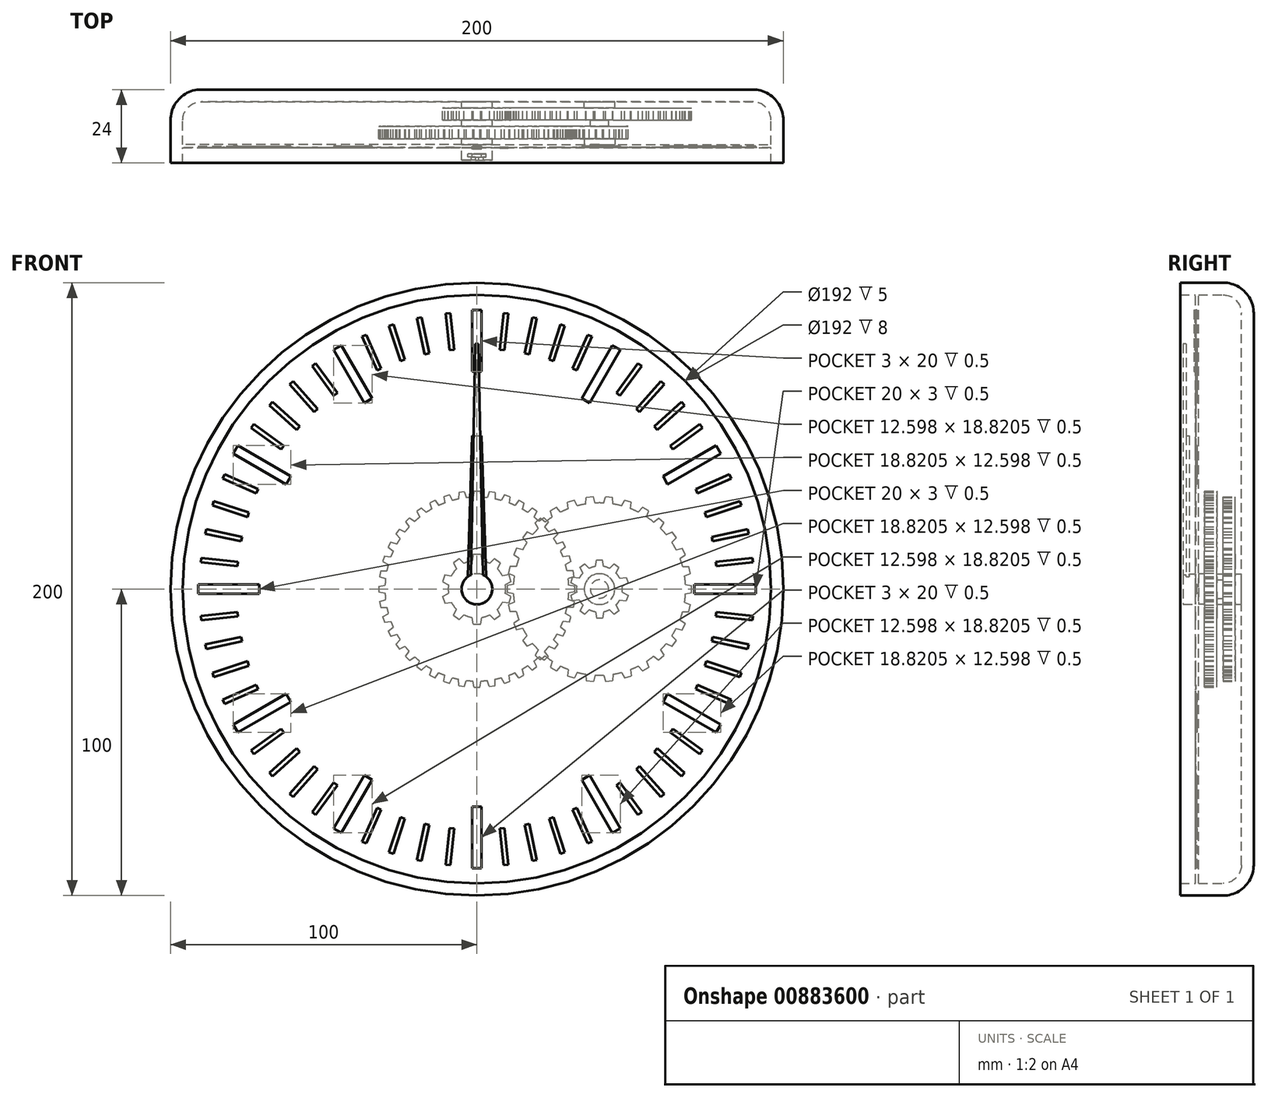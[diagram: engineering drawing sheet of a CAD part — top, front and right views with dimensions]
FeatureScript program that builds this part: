
annotation { "Feature Type Name" : "Feature", "Feature Type Description" : "" }
export const myFeature = defineFeature(function(context is Context, id is Id, definition is map)
    precondition{}
    {
        {
            var Q0;
            Q0=qCreatedBy(makeId("Front.planeOp"),FACE);
            var sketch = newSketch(context, id + "F0", { "sketchPlane" : qUnion([Q0])});
            skCircle(sketch, "E0", {"center": v(0, 0) * mm, "radius": 100 * mm});
            skSolve(sketch);
        }
        {
            var Q0;
            Q0 = qSketchRegion(id + "F0", true);
            extrude(context, id + "F1", {"entities" : qUnion([Q0]), "depth" : 24 * mm, "offsetDistance" : 25 * mm});
        }
        {
            var Q0;
            Q0=makeQuery(id+"F1.opExtrude","CAP_EDGE",EDGE,{"disambiguationData":[OSD([sQuery(id+"F0.wireOp",EDGE,"E0")])],"isStart":true});
            fillet(context, id + "F2", {"entities" : qUnion([Q0]), "radius" : 10 * mm, "tangentPropagation" : true, "allowEdgeOverflow" : false});
        }
        {
            var Q0;
            Q0=makeQuery(id+"F1.opExtrude","CAP_FACE",FACE,{"disambiguationData":[OSD([sQuery(id+"F0.wireOp",EDGE,"E0")])],"isStart":false});
            shell(context, id + "F3", {"entities" : qUnion([Q0]), "thickness" : 4 * mm});
        }
        {
            var Q0;
            {var subQ0=sQuery(id+"F0.wireOp",EDGE,"E0");Q0=makeQuery(id+"F3.opShell","OFFSET_FACE",FACE,{"disambiguationData":[OSD([subQ0]),TDD([makeQuery(id+"F1.opExtrude","CAP_FACE",FACE,{"disambiguationData":[OSD([subQ0])],"isStart":true})])]});}
            var sketch = newSketch(context, id + "F4", { "sketchPlane" : qUnion([Q0])});
            skCircle(sketch, "E1", {"center": v(0, 0) * mm, "radius": 3 * mm});
            skCircle(sketch, "E2", {"center": v(0, 0) * mm, "radius": 5 * mm});
            skCircle(sketch, "E3", {"center": v(40, 0) * mm, "radius": 3 * mm});
            skCircle(sketch, "E4", {"center": v(40, 0) * mm, "radius": 5 * mm});
            skSolve(sketch);
        }
        {
            var Q0;
            Q0 = qSketchRegion(id + "F4", true);
            extrude(context, id + "F5", {"entities" : qUnion([Q0]), "operationType" : NewBodyOperationType.ADD, "depth" : 2 * mm, "offsetDistance" : 25 * mm});
        }
        {
            var Q0;
            {var subQ0=sQuery(id+"F0.wireOp",EDGE,"E0");Q0=makeQuery(id+"F5.boolean.opBoolean","SPLIT",FACE,{"disambiguationData":[TD([makeQuery(id+"F5.opExtrude","SWEPT_FACE",FACE,{"disambiguationData":[OSD([sQuery(id+"F4.wireOp",EDGE,"E1")])]})])],"derivedFrom":makeQuery(id+"F3.opShell","OFFSET_FACE",FACE,{"disambiguationData":[OSD([subQ0]),TDD([makeQuery(id+"F1.opExtrude","CAP_FACE",FACE,{"disambiguationData":[OSD([subQ0])],"isStart":true})])]})});}
            extrude(context, id + "F6", {"entities" : qUnion([Q0]), "depth" : 19 * mm, "offsetDistance" : 25 * mm});
        }
        {
            var Q0;
            {var subQ0=sQuery(id+"F0.wireOp",EDGE,"E0");Q0=makeQuery(id+"F5.boolean.opBoolean","SPLIT",FACE,{"disambiguationData":[TD([makeQuery(id+"F5.opExtrude","SWEPT_FACE",FACE,{"disambiguationData":[OSD([sQuery(id+"F4.wireOp",EDGE,"E3")])]})])],"derivedFrom":makeQuery(id+"F3.opShell","OFFSET_FACE",FACE,{"disambiguationData":[OSD([subQ0]),TDD([makeQuery(id+"F1.opExtrude","CAP_FACE",FACE,{"disambiguationData":[OSD([subQ0])],"isStart":true})])]})});}
            extrude(context, id + "F7", {"entities" : qUnion([Q0]), "depth" : 8 * mm, "offsetDistance" : 25 * mm});
        }
        {
            var Q0;
            Q0=makeQuery(id+"F5.opExtrude","CAP_FACE",FACE,{"disambiguationData":[OSD([sQuery(id+"F4.wireOp",EDGE,"E1"),sQuery(id+"F4.wireOp",EDGE,"E2")])],"isStart":false});
            var sketch = newSketch(context, id + "F8", { "sketchPlane" : qUnion([Q0])});
            skCircle(sketch, "E5", {"center": v(0, 0) * mm, "radius": 9.38 * mm});
            skLineSegment(sketch, "E6", {"start": v(0, 11.38) * mm, "end": v(1.18, 11.38) * mm});
            skLineSegment(sketch, "E7", {"start": v(1.18, 11.38) * mm, "end": v(1.55, 9.25) * mm});
            skLineSegment(sketch, "E8.MirrorCS", {"start": v(0, 11.38) * mm, "end": v(-1.18, 11.38) * mm});
            skLineSegment(sketch, "E9.MirrorCS", {"start": v(-1.18, 11.38) * mm, "end": v(-1.55, 9.25) * mm});
            skLineSegment(sketch, "E10.1.0", {"start": v(-7.64, 8.51) * mm, "end": v(-6.7, 6.57) * mm});
            skLineSegment(sketch, "E10.1.1", {"start": v(-6.69, 9.2) * mm, "end": v(-7.64, 8.51) * mm});
            skLineSegment(sketch, "E10.1.2", {"start": v(-6.69, 9.2) * mm, "end": v(-5.73, 9.9) * mm});
            skLineSegment(sketch, "E10.1.3", {"start": v(-5.73, 9.9) * mm, "end": v(-4.18, 8.4) * mm});
            skLineSegment(sketch, "E10.2.0", {"start": v(-11.18, 2.4) * mm, "end": v(-9.27, 1.38) * mm});
            skLineSegment(sketch, "E10.2.1", {"start": v(-10.82, 3.52) * mm, "end": v(-11.18, 2.4) * mm});
            skLineSegment(sketch, "E10.2.2", {"start": v(-10.82, 3.52) * mm, "end": v(-10.45, 4.64) * mm});
            skLineSegment(sketch, "E10.2.3", {"start": v(-10.45, 4.64) * mm, "end": v(-8.31, 4.33) * mm});
            skLineSegment(sketch, "E11.2.3.0", {"start": v(-10.45, -4.64) * mm, "end": v(-8.31, -4.33) * mm});
            skLineSegment(sketch, "E11.3.3.0", {"start": v(-10.82, -3.52) * mm, "end": v(-10.45, -4.64) * mm});
            skLineSegment(sketch, "E11.6.3.0", {"start": v(-10.82, -3.52) * mm, "end": v(-11.18, -2.4) * mm});
            skLineSegment(sketch, "E11.9.3.0", {"start": v(-11.18, -2.4) * mm, "end": v(-9.27, -1.38) * mm});
            skLineSegment(sketch, "E11.2.4.0", {"start": v(-5.73, -9.9) * mm, "end": v(-4.18, -8.4) * mm});
            skLineSegment(sketch, "E11.3.4.0", {"start": v(-6.69, -9.2) * mm, "end": v(-5.73, -9.9) * mm});
            skLineSegment(sketch, "E11.6.4.0", {"start": v(-6.69, -9.2) * mm, "end": v(-7.64, -8.51) * mm});
            skLineSegment(sketch, "E11.9.4.0", {"start": v(-7.64, -8.51) * mm, "end": v(-6.7, -6.57) * mm});
            skLineSegment(sketch, "E11.2.5.0", {"start": v(1.18, -11.38) * mm, "end": v(1.55, -9.25) * mm});
            skLineSegment(sketch, "E11.3.5.0", {"start": v(0, -11.38) * mm, "end": v(1.18, -11.38) * mm});
            skLineSegment(sketch, "E11.6.5.0", {"start": v(0, -11.38) * mm, "end": v(-1.18, -11.38) * mm});
            skLineSegment(sketch, "E11.9.5.0", {"start": v(-1.18, -11.38) * mm, "end": v(-1.55, -9.25) * mm});
            skLineSegment(sketch, "E11.2.6.0", {"start": v(7.64, -8.51) * mm, "end": v(6.7, -6.57) * mm});
            skLineSegment(sketch, "E11.3.6.0", {"start": v(6.69, -9.2) * mm, "end": v(7.64, -8.51) * mm});
            skLineSegment(sketch, "E11.6.6.0", {"start": v(6.69, -9.2) * mm, "end": v(5.73, -9.9) * mm});
            skLineSegment(sketch, "E11.9.6.0", {"start": v(5.73, -9.9) * mm, "end": v(4.18, -8.4) * mm});
            skLineSegment(sketch, "E11.2.7.0", {"start": v(11.18, -2.4) * mm, "end": v(9.27, -1.38) * mm});
            skLineSegment(sketch, "E11.3.7.0", {"start": v(10.82, -3.52) * mm, "end": v(11.18, -2.4) * mm});
            skLineSegment(sketch, "E11.6.7.0", {"start": v(10.82, -3.52) * mm, "end": v(10.45, -4.64) * mm});
            skLineSegment(sketch, "E11.9.7.0", {"start": v(10.45, -4.64) * mm, "end": v(8.31, -4.33) * mm});
            skLineSegment(sketch, "E11.2.8.0", {"start": v(10.45, 4.64) * mm, "end": v(8.31, 4.33) * mm});
            skLineSegment(sketch, "E11.3.8.0", {"start": v(10.82, 3.52) * mm, "end": v(10.45, 4.64) * mm});
            skLineSegment(sketch, "E11.6.8.0", {"start": v(10.82, 3.52) * mm, "end": v(11.18, 2.4) * mm});
            skLineSegment(sketch, "E11.9.8.0", {"start": v(11.18, 2.4) * mm, "end": v(9.27, 1.38) * mm});
            skLineSegment(sketch, "E11.2.9.0", {"start": v(5.73, 9.9) * mm, "end": v(4.18, 8.4) * mm});
            skLineSegment(sketch, "E11.3.9.0", {"start": v(6.69, 9.2) * mm, "end": v(5.73, 9.9) * mm});
            skLineSegment(sketch, "E11.6.9.0", {"start": v(6.69, 9.2) * mm, "end": v(7.64, 8.51) * mm});
            skLineSegment(sketch, "E11.9.9.0", {"start": v(7.64, 8.51) * mm, "end": v(6.7, 6.57) * mm});
            skSolve(sketch);
        }
        {
            var Q0;
            Q0 = qSketchRegion(id + "F8", true);
            extrude(context, id + "F9", {"entities" : qUnion([Q0]), "operationType" : NewBodyOperationType.ADD, "depth" : 4 * mm, "offsetDistance" : 25 * mm});
        }
        {
            var Q0;
            Q0=makeQuery(id+"F5.opExtrude","CAP_FACE",FACE,{"disambiguationData":[OSD([sQuery(id+"F4.wireOp",EDGE,"E3"),sQuery(id+"F4.wireOp",EDGE,"E4")])],"isStart":false});
            var sketch = newSketch(context, id + "F10", { "sketchPlane" : qUnion([Q0])});
            skCircle(sketch, "E12", {"center": v(40, 0) * mm, "radius": 28.12 * mm});
            skLineSegment(sketch, "E13", {"start": v(11.92, 1.54) * mm, "end": v(9.88, 1.18) * mm});
            skLineSegment(sketch, "E14", {"start": v(9.88, 1.18) * mm, "end": v(9.88, 0) * mm});
            skLineSegment(sketch, "E15.MirrorCS", {"start": v(9.88, -1.18) * mm, "end": v(9.88, 0) * mm});
            skLineSegment(sketch, "E16.MirrorCS", {"start": v(11.92, -1.54) * mm, "end": v(9.88, -1.18) * mm});
            skLineSegment(sketch, "E17.1.0", {"start": v(12.85, -7.34) * mm, "end": v(10.78, -7.42) * mm});
            skLineSegment(sketch, "E17.1.1", {"start": v(10.78, -7.42) * mm, "end": v(10.53, -6.26) * mm});
            skLineSegment(sketch, "E17.1.2", {"start": v(10.29, -5.11) * mm, "end": v(10.53, -6.26) * mm});
            skLineSegment(sketch, "E17.1.3", {"start": v(12.21, -4.33) * mm, "end": v(10.29, -5.11) * mm});
            skLineSegment(sketch, "E17.2.0", {"start": v(14.97, -12.83) * mm, "end": v(12.96, -13.33) * mm});
            skLineSegment(sketch, "E17.2.1", {"start": v(12.96, -13.33) * mm, "end": v(12.48, -12.25) * mm});
            skLineSegment(sketch, "E17.2.2", {"start": v(12, -11.18) * mm, "end": v(12.48, -12.25) * mm});
            skLineSegment(sketch, "E17.2.3", {"start": v(13.72, -10.02) * mm, "end": v(12, -11.18) * mm});
            skLineSegment(sketch, "E18.2.3.0", {"start": v(18.18, -17.75) * mm, "end": v(16.32, -18.66) * mm});
            skLineSegment(sketch, "E18.3.3.0", {"start": v(16.32, -18.66) * mm, "end": v(15.63, -17.7) * mm});
            skLineSegment(sketch, "E18.6.3.0", {"start": v(14.94, -16.75) * mm, "end": v(15.63, -17.7) * mm});
            skLineSegment(sketch, "E18.9.3.0", {"start": v(16.38, -15.26) * mm, "end": v(14.94, -16.75) * mm});
            skLineSegment(sketch, "E18.2.4.0", {"start": v(22.35, -21.9) * mm, "end": v(20.72, -23.18) * mm});
            skLineSegment(sketch, "E18.3.4.0", {"start": v(20.72, -23.18) * mm, "end": v(19.84, -22.39) * mm});
            skLineSegment(sketch, "E18.6.4.0", {"start": v(18.97, -21.6) * mm, "end": v(19.84, -22.39) * mm});
            skLineSegment(sketch, "E18.9.4.0", {"start": v(20.07, -19.84) * mm, "end": v(18.97, -21.6) * mm});
            skLineSegment(sketch, "E18.2.5.0", {"start": v(27.3, -25.09) * mm, "end": v(25.96, -26.68) * mm});
            skLineSegment(sketch, "E18.3.5.0", {"start": v(25.96, -26.68) * mm, "end": v(24.94, -26.09) * mm});
            skLineSegment(sketch, "E18.6.5.0", {"start": v(23.92, -25.5) * mm, "end": v(24.94, -26.09) * mm});
            skLineSegment(sketch, "E18.9.5.0", {"start": v(24.63, -23.55) * mm, "end": v(23.92, -25.5) * mm});
            skLineSegment(sketch, "E18.2.6.0", {"start": v(32.78, -27.18) * mm, "end": v(31.81, -29.01) * mm});
            skLineSegment(sketch, "E18.3.6.0", {"start": v(31.81, -29.01) * mm, "end": v(30.7, -28.65) * mm});
            skLineSegment(sketch, "E18.6.6.0", {"start": v(29.57, -28.29) * mm, "end": v(30.7, -28.65) * mm});
            skLineSegment(sketch, "E18.9.6.0", {"start": v(29.86, -26.23) * mm, "end": v(29.57, -28.29) * mm});
            skLineSegment(sketch, "E18.2.7.0", {"start": v(38.6, -28.09) * mm, "end": v(38.02, -30.08) * mm});
            skLineSegment(sketch, "E18.3.7.0", {"start": v(38.02, -30.08) * mm, "end": v(36.85, -29.96) * mm});
            skLineSegment(sketch, "E18.6.7.0", {"start": v(35.68, -29.84) * mm, "end": v(36.85, -29.96) * mm});
            skLineSegment(sketch, "E18.9.7.0", {"start": v(35.53, -27.77) * mm, "end": v(35.68, -29.84) * mm});
            skLineSegment(sketch, "E18.2.8.0", {"start": v(44.47, -27.77) * mm, "end": v(44.32, -29.84) * mm});
            skLineSegment(sketch, "E18.3.8.0", {"start": v(44.32, -29.84) * mm, "end": v(43.15, -29.96) * mm});
            skLineSegment(sketch, "E18.6.8.0", {"start": v(41.98, -30.08) * mm, "end": v(43.15, -29.96) * mm});
            skLineSegment(sketch, "E18.9.8.0", {"start": v(41.4, -28.09) * mm, "end": v(41.98, -30.08) * mm});
            skLineSegment(sketch, "E18.2.9.0", {"start": v(50.14, -26.23) * mm, "end": v(50.43, -28.29) * mm});
            skLineSegment(sketch, "E18.3.9.0", {"start": v(50.43, -28.29) * mm, "end": v(49.3, -28.65) * mm});
            skLineSegment(sketch, "E18.6.9.0", {"start": v(48.19, -29.01) * mm, "end": v(49.3, -28.65) * mm});
            skLineSegment(sketch, "E18.9.9.0", {"start": v(47.22, -27.18) * mm, "end": v(48.19, -29.01) * mm});
            skLineSegment(sketch, "E18.2.10.0", {"start": v(55.37, -23.55) * mm, "end": v(56.08, -25.5) * mm});
            skLineSegment(sketch, "E18.3.10.0", {"start": v(56.08, -25.5) * mm, "end": v(55.06, -26.09) * mm});
            skLineSegment(sketch, "E18.6.10.0", {"start": v(54.04, -26.68) * mm, "end": v(55.06, -26.09) * mm});
            skLineSegment(sketch, "E18.9.10.0", {"start": v(52.7, -25.09) * mm, "end": v(54.04, -26.68) * mm});
            skLineSegment(sketch, "E18.2.11.0", {"start": v(59.93, -19.84) * mm, "end": v(61.03, -21.6) * mm});
            skLineSegment(sketch, "E18.3.11.0", {"start": v(61.03, -21.6) * mm, "end": v(60.16, -22.39) * mm});
            skLineSegment(sketch, "E18.6.11.0", {"start": v(59.28, -23.18) * mm, "end": v(60.16, -22.39) * mm});
            skLineSegment(sketch, "E18.9.11.0", {"start": v(57.65, -21.9) * mm, "end": v(59.28, -23.18) * mm});
            skLineSegment(sketch, "E18.2.12.0", {"start": v(63.62, -15.26) * mm, "end": v(65.06, -16.75) * mm});
            skLineSegment(sketch, "E18.3.12.0", {"start": v(65.06, -16.75) * mm, "end": v(64.37, -17.7) * mm});
            skLineSegment(sketch, "E18.6.12.0", {"start": v(63.68, -18.66) * mm, "end": v(64.37, -17.7) * mm});
            skLineSegment(sketch, "E18.9.12.0", {"start": v(61.82, -17.75) * mm, "end": v(63.68, -18.66) * mm});
            skLineSegment(sketch, "E18.2.13.0", {"start": v(66.28, -10.02) * mm, "end": v(68, -11.18) * mm});
            skLineSegment(sketch, "E18.3.13.0", {"start": v(68, -11.18) * mm, "end": v(67.52, -12.25) * mm});
            skLineSegment(sketch, "E18.6.13.0", {"start": v(67.04, -13.33) * mm, "end": v(67.52, -12.25) * mm});
            skLineSegment(sketch, "E18.9.13.0", {"start": v(65.03, -12.83) * mm, "end": v(67.04, -13.33) * mm});
            skLineSegment(sketch, "E18.2.14.0", {"start": v(67.79, -4.33) * mm, "end": v(69.71, -5.11) * mm});
            skLineSegment(sketch, "E18.3.14.0", {"start": v(69.71, -5.11) * mm, "end": v(69.47, -6.26) * mm});
            skLineSegment(sketch, "E18.6.14.0", {"start": v(69.22, -7.42) * mm, "end": v(69.47, -6.26) * mm});
            skLineSegment(sketch, "E18.9.14.0", {"start": v(67.15, -7.34) * mm, "end": v(69.22, -7.42) * mm});
            skLineSegment(sketch, "E18.2.15.0", {"start": v(68.08, 1.54) * mm, "end": v(70.13, 1.18) * mm});
            skLineSegment(sketch, "E18.3.15.0", {"start": v(70.12, 1.18) * mm, "end": v(70.12, 0) * mm});
            skLineSegment(sketch, "E18.6.15.0", {"start": v(70.12, -1.18) * mm, "end": v(70.12, 0) * mm});
            skLineSegment(sketch, "E18.9.15.0", {"start": v(68.08, -1.54) * mm, "end": v(70.13, -1.18) * mm});
            skLineSegment(sketch, "E18.2.16.0", {"start": v(67.15, 7.34) * mm, "end": v(69.22, 7.42) * mm});
            skLineSegment(sketch, "E18.3.16.0", {"start": v(69.22, 7.42) * mm, "end": v(69.47, 6.26) * mm});
            skLineSegment(sketch, "E18.6.16.0", {"start": v(69.71, 5.11) * mm, "end": v(69.47, 6.26) * mm});
            skLineSegment(sketch, "E18.9.16.0", {"start": v(67.79, 4.33) * mm, "end": v(69.71, 5.11) * mm});
            skLineSegment(sketch, "E18.2.17.0", {"start": v(65.03, 12.83) * mm, "end": v(67.04, 13.33) * mm});
            skLineSegment(sketch, "E18.3.17.0", {"start": v(67.04, 13.33) * mm, "end": v(67.52, 12.25) * mm});
            skLineSegment(sketch, "E18.6.17.0", {"start": v(68, 11.18) * mm, "end": v(67.52, 12.25) * mm});
            skLineSegment(sketch, "E18.9.17.0", {"start": v(66.28, 10.02) * mm, "end": v(68, 11.18) * mm});
            skLineSegment(sketch, "E18.2.18.0", {"start": v(61.82, 17.75) * mm, "end": v(63.68, 18.66) * mm});
            skLineSegment(sketch, "E18.3.18.0", {"start": v(63.68, 18.66) * mm, "end": v(64.37, 17.7) * mm});
            skLineSegment(sketch, "E18.6.18.0", {"start": v(65.06, 16.75) * mm, "end": v(64.37, 17.7) * mm});
            skLineSegment(sketch, "E18.9.18.0", {"start": v(63.62, 15.26) * mm, "end": v(65.06, 16.75) * mm});
            skLineSegment(sketch, "E18.2.19.0", {"start": v(57.65, 21.9) * mm, "end": v(59.28, 23.18) * mm});
            skLineSegment(sketch, "E18.3.19.0", {"start": v(59.28, 23.18) * mm, "end": v(60.16, 22.39) * mm});
            skLineSegment(sketch, "E18.6.19.0", {"start": v(61.03, 21.6) * mm, "end": v(60.16, 22.39) * mm});
            skLineSegment(sketch, "E18.9.19.0", {"start": v(59.93, 19.84) * mm, "end": v(61.03, 21.6) * mm});
            skLineSegment(sketch, "E18.2.20.0", {"start": v(52.7, 25.09) * mm, "end": v(54.04, 26.68) * mm});
            skLineSegment(sketch, "E18.3.20.0", {"start": v(54.04, 26.68) * mm, "end": v(55.06, 26.09) * mm});
            skLineSegment(sketch, "E18.6.20.0", {"start": v(56.08, 25.5) * mm, "end": v(55.06, 26.09) * mm});
            skLineSegment(sketch, "E18.9.20.0", {"start": v(55.37, 23.55) * mm, "end": v(56.08, 25.5) * mm});
            skLineSegment(sketch, "E18.2.21.0", {"start": v(47.22, 27.18) * mm, "end": v(48.19, 29.01) * mm});
            skLineSegment(sketch, "E18.3.21.0", {"start": v(48.19, 29.01) * mm, "end": v(49.3, 28.65) * mm});
            skLineSegment(sketch, "E18.6.21.0", {"start": v(50.43, 28.29) * mm, "end": v(49.3, 28.65) * mm});
            skLineSegment(sketch, "E18.9.21.0", {"start": v(50.14, 26.23) * mm, "end": v(50.43, 28.29) * mm});
            skLineSegment(sketch, "E18.2.22.0", {"start": v(41.4, 28.09) * mm, "end": v(41.98, 30.08) * mm});
            skLineSegment(sketch, "E18.3.22.0", {"start": v(41.98, 30.08) * mm, "end": v(43.15, 29.96) * mm});
            skLineSegment(sketch, "E18.6.22.0", {"start": v(44.32, 29.84) * mm, "end": v(43.15, 29.96) * mm});
            skLineSegment(sketch, "E18.9.22.0", {"start": v(44.47, 27.77) * mm, "end": v(44.32, 29.84) * mm});
            skLineSegment(sketch, "E18.2.23.0", {"start": v(35.53, 27.77) * mm, "end": v(35.68, 29.84) * mm});
            skLineSegment(sketch, "E18.3.23.0", {"start": v(35.68, 29.84) * mm, "end": v(36.85, 29.96) * mm});
            skLineSegment(sketch, "E18.6.23.0", {"start": v(38.02, 30.08) * mm, "end": v(36.85, 29.96) * mm});
            skLineSegment(sketch, "E18.9.23.0", {"start": v(38.6, 28.09) * mm, "end": v(38.02, 30.08) * mm});
            skLineSegment(sketch, "E18.2.24.0", {"start": v(29.86, 26.23) * mm, "end": v(29.57, 28.29) * mm});
            skLineSegment(sketch, "E18.3.24.0", {"start": v(29.57, 28.29) * mm, "end": v(30.7, 28.65) * mm});
            skLineSegment(sketch, "E18.6.24.0", {"start": v(31.81, 29.01) * mm, "end": v(30.7, 28.65) * mm});
            skLineSegment(sketch, "E18.9.24.0", {"start": v(32.78, 27.18) * mm, "end": v(31.81, 29.01) * mm});
            skLineSegment(sketch, "E18.2.25.0", {"start": v(24.63, 23.55) * mm, "end": v(23.92, 25.5) * mm});
            skLineSegment(sketch, "E18.3.25.0", {"start": v(23.92, 25.5) * mm, "end": v(24.94, 26.09) * mm});
            skLineSegment(sketch, "E18.6.25.0", {"start": v(25.96, 26.68) * mm, "end": v(24.94, 26.09) * mm});
            skLineSegment(sketch, "E18.9.25.0", {"start": v(27.3, 25.09) * mm, "end": v(25.96, 26.68) * mm});
            skLineSegment(sketch, "E18.2.26.0", {"start": v(20.07, 19.84) * mm, "end": v(18.97, 21.6) * mm});
            skLineSegment(sketch, "E18.3.26.0", {"start": v(18.97, 21.6) * mm, "end": v(19.84, 22.39) * mm});
            skLineSegment(sketch, "E18.6.26.0", {"start": v(20.72, 23.18) * mm, "end": v(19.84, 22.39) * mm});
            skLineSegment(sketch, "E18.9.26.0", {"start": v(22.35, 21.9) * mm, "end": v(20.72, 23.18) * mm});
            skLineSegment(sketch, "E18.2.27.0", {"start": v(16.38, 15.26) * mm, "end": v(14.94, 16.75) * mm});
            skLineSegment(sketch, "E18.3.27.0", {"start": v(14.94, 16.75) * mm, "end": v(15.63, 17.7) * mm});
            skLineSegment(sketch, "E18.6.27.0", {"start": v(16.32, 18.66) * mm, "end": v(15.63, 17.7) * mm});
            skLineSegment(sketch, "E18.9.27.0", {"start": v(18.18, 17.75) * mm, "end": v(16.32, 18.66) * mm});
            skLineSegment(sketch, "E18.2.28.0", {"start": v(13.72, 10.02) * mm, "end": v(12, 11.18) * mm});
            skLineSegment(sketch, "E18.3.28.0", {"start": v(12, 11.18) * mm, "end": v(12.48, 12.25) * mm});
            skLineSegment(sketch, "E18.6.28.0", {"start": v(12.96, 13.33) * mm, "end": v(12.48, 12.25) * mm});
            skLineSegment(sketch, "E18.9.28.0", {"start": v(14.97, 12.83) * mm, "end": v(12.96, 13.33) * mm});
            skLineSegment(sketch, "E18.2.29.0", {"start": v(12.21, 4.33) * mm, "end": v(10.29, 5.11) * mm});
            skLineSegment(sketch, "E18.3.29.0", {"start": v(10.29, 5.11) * mm, "end": v(10.53, 6.26) * mm});
            skLineSegment(sketch, "E18.6.29.0", {"start": v(10.78, 7.42) * mm, "end": v(10.53, 6.26) * mm});
            skLineSegment(sketch, "E18.9.29.0", {"start": v(12.85, 7.34) * mm, "end": v(10.78, 7.42) * mm});
            skSolve(sketch);
        }
        {
            var Q0;
            Q0 = qSketchRegion(id + "F10", true);
            extrude(context, id + "F11", {"entities" : qUnion([Q0]), "operationType" : NewBodyOperationType.ADD, "depth" : 4 * mm, "offsetDistance" : 25 * mm});
        }
        {
            var Q0;
            Q0=makeQuery(id+"F9.opExtrude","CAP_FACE",FACE,{"disambiguationData":[OSD([sQuery(id+"F8.wireOp",EDGE,"E5"),sQuery(id+"F8.wireOp",EDGE,"E6"),sQuery(id+"F8.wireOp",EDGE,"E7"),sQuery(id+"F8.wireOp",EDGE,"E8.MirrorCS"),sQuery(id+"F8.wireOp",EDGE,"E9.MirrorCS"),sQuery(id+"F8.wireOp",EDGE,"E10.1.0"),sQuery(id+"F8.wireOp",EDGE,"E10.1.1"),sQuery(id+"F8.wireOp",EDGE,"E10.1.2"),sQuery(id+"F8.wireOp",EDGE,"E10.1.3"),sQuery(id+"F8.wireOp",EDGE,"E10.2.0"),sQuery(id+"F8.wireOp",EDGE,"E10.2.1"),sQuery(id+"F8.wireOp",EDGE,"E10.2.2"),sQuery(id+"F8.wireOp",EDGE,"E10.2.3"),sQuery(id+"F8.wireOp",EDGE,"E11.2.3.0"),sQuery(id+"F8.wireOp",EDGE,"E11.3.3.0"),sQuery(id+"F8.wireOp",EDGE,"E11.6.3.0"),sQuery(id+"F8.wireOp",EDGE,"E11.9.3.0"),sQuery(id+"F8.wireOp",EDGE,"E11.2.4.0"),sQuery(id+"F8.wireOp",EDGE,"E11.3.4.0"),sQuery(id+"F8.wireOp",EDGE,"E11.6.4.0"),sQuery(id+"F8.wireOp",EDGE,"E11.9.4.0"),sQuery(id+"F8.wireOp",EDGE,"E11.2.5.0"),sQuery(id+"F8.wireOp",EDGE,"E11.3.5.0"),sQuery(id+"F8.wireOp",EDGE,"E11.6.5.0"),sQuery(id+"F8.wireOp",EDGE,"E11.9.5.0"),sQuery(id+"F8.wireOp",EDGE,"E11.2.6.0"),sQuery(id+"F8.wireOp",EDGE,"E11.3.6.0"),sQuery(id+"F8.wireOp",EDGE,"E11.6.6.0"),sQuery(id+"F8.wireOp",EDGE,"E11.9.6.0"),sQuery(id+"F8.wireOp",EDGE,"E11.2.7.0"),sQuery(id+"F8.wireOp",EDGE,"E11.3.7.0"),sQuery(id+"F8.wireOp",EDGE,"E11.6.7.0"),sQuery(id+"F8.wireOp",EDGE,"E11.9.7.0"),sQuery(id+"F8.wireOp",EDGE,"E11.2.8.0"),sQuery(id+"F8.wireOp",EDGE,"E11.3.8.0"),sQuery(id+"F8.wireOp",EDGE,"E11.6.8.0"),sQuery(id+"F8.wireOp",EDGE,"E11.9.8.0"),sQuery(id+"F8.wireOp",EDGE,"E11.2.9.0"),sQuery(id+"F8.wireOp",EDGE,"E11.3.9.0"),sQuery(id+"F8.wireOp",EDGE,"E11.6.9.0"),sQuery(id+"F8.wireOp",EDGE,"E11.9.9.0")])],"isStart":false});
            var sketch = newSketch(context, id + "F12", { "sketchPlane" : qUnion([Q0])});
            skCircle(sketch, "E19.0", {"center": v(0, 0) * mm, "radius": 3 * mm});
            skCircle(sketch, "E20.0", {"center": v(0, 0) * mm, "radius": 5 * mm});
            skSolve(sketch);
        }
        {
            var Q0;
            Q0 = qSketchRegion(id + "F12", true);
            extrude(context, id + "F13", {"entities" : qUnion([Q0]), "depth" : 2 * mm, "offsetDistance" : 25 * mm});
        }
        {
            var Q0;
            Q0=makeQuery(id+"F13.opExtrude","CAP_FACE",FACE,{"disambiguationData":[OSD([sQuery(id+"F12.wireOp",EDGE,"E19.0"),sQuery(id+"F12.wireOp",EDGE,"E20.0")])],"isStart":false});
            var sketch = newSketch(context, id + "F14", { "sketchPlane" : qUnion([Q0])});
            skCircle(sketch, "E21.0.0", {"center": v(0, 0) * mm, "radius": 3 * mm});
            skCircle(sketch, "E22", {"center": v(0, 0) * mm, "radius": 30 * mm});
            skLineSegment(sketch, "E23", {"start": v(0, 32) * mm, "end": v(0.94, 32) * mm});
            skLineSegment(sketch, "E24", {"start": v(0.94, 32) * mm, "end": v(1.3, 29.97) * mm});
            skLineSegment(sketch, "E25.MirrorCS", {"start": v(0, 32) * mm, "end": v(-0.94, 32) * mm});
            skLineSegment(sketch, "E26.MirrorCS", {"start": v(-0.94, 32) * mm, "end": v(-1.3, 29.97) * mm});
            skLineSegment(sketch, "E27.1.0", {"start": v(-5.94, 31.46) * mm, "end": v(-5.97, 29.4) * mm});
            skLineSegment(sketch, "E27.1.1", {"start": v(-5, 31.6) * mm, "end": v(-5.94, 31.46) * mm});
            skLineSegment(sketch, "E27.1.2", {"start": v(-5, 31.6) * mm, "end": v(-4.08, 31.75) * mm});
            skLineSegment(sketch, "E27.1.3", {"start": v(-4.08, 31.75) * mm, "end": v(-3.4, 29.8) * mm});
            skLineSegment(sketch, "E27.2.0", {"start": v(-10.78, 30.14) * mm, "end": v(-10.5, 28.1) * mm});
            skLineSegment(sketch, "E27.2.1", {"start": v(-9.89, 30.43) * mm, "end": v(-10.78, 30.14) * mm});
            skLineSegment(sketch, "E27.2.2", {"start": v(-9.89, 30.43) * mm, "end": v(-9, 30.73) * mm});
            skLineSegment(sketch, "E27.2.3", {"start": v(-9, 30.73) * mm, "end": v(-8.03, 28.9) * mm});
            skLineSegment(sketch, "E28.2.3.0", {"start": v(-15.37, 28.08) * mm, "end": v(-14.77, 26.11) * mm});
            skLineSegment(sketch, "E28.3.3.0", {"start": v(-14.53, 28.51) * mm, "end": v(-15.37, 28.08) * mm});
            skLineSegment(sketch, "E28.6.3.0", {"start": v(-14.53, 28.51) * mm, "end": v(-13.69, 28.94) * mm});
            skLineSegment(sketch, "E28.9.3.0", {"start": v(-13.69, 28.94) * mm, "end": v(-12.45, 27.3) * mm});
            skLineSegment(sketch, "E28.2.4.0", {"start": v(-19.57, 25.33) * mm, "end": v(-18.67, 23.48) * mm});
            skLineSegment(sketch, "E28.3.4.0", {"start": v(-18.8, 25.89) * mm, "end": v(-19.57, 25.33) * mm});
            skLineSegment(sketch, "E28.6.4.0", {"start": v(-18.8, 25.89) * mm, "end": v(-18.05, 26.44) * mm});
            skLineSegment(sketch, "E28.9.4.0", {"start": v(-18.05, 26.44) * mm, "end": v(-16.57, 25.01) * mm});
            skLineSegment(sketch, "E28.2.5.0", {"start": v(-23.3, 21.96) * mm, "end": v(-22.11, 20.27) * mm});
            skLineSegment(sketch, "E28.3.5.0", {"start": v(-22.63, 22.63) * mm, "end": v(-23.3, 21.96) * mm});
            skLineSegment(sketch, "E28.6.5.0", {"start": v(-22.63, 22.63) * mm, "end": v(-21.96, 23.3) * mm});
            skLineSegment(sketch, "E28.9.5.0", {"start": v(-21.96, 23.3) * mm, "end": v(-20.27, 22.11) * mm});
            skLineSegment(sketch, "E28.2.6.0", {"start": v(-26.44, 18.05) * mm, "end": v(-25.01, 16.57) * mm});
            skLineSegment(sketch, "E28.3.6.0", {"start": v(-25.89, 18.8) * mm, "end": v(-26.44, 18.05) * mm});
            skLineSegment(sketch, "E28.6.6.0", {"start": v(-25.89, 18.8) * mm, "end": v(-25.33, 19.57) * mm});
            skLineSegment(sketch, "E28.9.6.0", {"start": v(-25.33, 19.57) * mm, "end": v(-23.48, 18.67) * mm});
            skLineSegment(sketch, "E28.2.7.0", {"start": v(-28.94, 13.69) * mm, "end": v(-27.3, 12.45) * mm});
            skLineSegment(sketch, "E28.3.7.0", {"start": v(-28.51, 14.53) * mm, "end": v(-28.94, 13.69) * mm});
            skLineSegment(sketch, "E28.6.7.0", {"start": v(-28.51, 14.53) * mm, "end": v(-28.08, 15.37) * mm});
            skLineSegment(sketch, "E28.9.7.0", {"start": v(-28.08, 15.37) * mm, "end": v(-26.11, 14.77) * mm});
            skLineSegment(sketch, "E28.2.8.0", {"start": v(-30.73, 9) * mm, "end": v(-28.9, 8.03) * mm});
            skLineSegment(sketch, "E28.3.8.0", {"start": v(-30.43, 9.89) * mm, "end": v(-30.73, 9) * mm});
            skLineSegment(sketch, "E28.6.8.0", {"start": v(-30.43, 9.89) * mm, "end": v(-30.14, 10.78) * mm});
            skLineSegment(sketch, "E28.9.8.0", {"start": v(-30.14, 10.78) * mm, "end": v(-28.1, 10.5) * mm});
            skLineSegment(sketch, "E28.2.9.0", {"start": v(-31.75, 4.08) * mm, "end": v(-29.8, 3.4) * mm});
            skLineSegment(sketch, "E28.3.9.0", {"start": v(-31.6, 5) * mm, "end": v(-31.75, 4.08) * mm});
            skLineSegment(sketch, "E28.6.9.0", {"start": v(-31.6, 5) * mm, "end": v(-31.46, 5.94) * mm});
            skLineSegment(sketch, "E28.9.9.0", {"start": v(-31.46, 5.94) * mm, "end": v(-29.4, 5.97) * mm});
            skLineSegment(sketch, "E28.2.10.0", {"start": v(-32, -0.94) * mm, "end": v(-29.97, -1.3) * mm});
            skLineSegment(sketch, "E28.3.10.0", {"start": v(-32, 0) * mm, "end": v(-32, -0.94) * mm});
            skLineSegment(sketch, "E28.6.10.0", {"start": v(-32, 0) * mm, "end": v(-32, 0.94) * mm});
            skLineSegment(sketch, "E28.9.10.0", {"start": v(-32, 0.94) * mm, "end": v(-29.97, 1.3) * mm});
            skLineSegment(sketch, "E28.2.11.0", {"start": v(-31.46, -5.94) * mm, "end": v(-29.4, -5.97) * mm});
            skLineSegment(sketch, "E28.3.11.0", {"start": v(-31.6, -5) * mm, "end": v(-31.46, -5.94) * mm});
            skLineSegment(sketch, "E28.6.11.0", {"start": v(-31.6, -5) * mm, "end": v(-31.75, -4.08) * mm});
            skLineSegment(sketch, "E28.9.11.0", {"start": v(-31.75, -4.08) * mm, "end": v(-29.8, -3.4) * mm});
            skLineSegment(sketch, "E28.2.12.0", {"start": v(-30.14, -10.78) * mm, "end": v(-28.1, -10.5) * mm});
            skLineSegment(sketch, "E28.3.12.0", {"start": v(-30.43, -9.89) * mm, "end": v(-30.14, -10.78) * mm});
            skLineSegment(sketch, "E28.6.12.0", {"start": v(-30.43, -9.89) * mm, "end": v(-30.73, -9) * mm});
            skLineSegment(sketch, "E28.9.12.0", {"start": v(-30.73, -9) * mm, "end": v(-28.9, -8.03) * mm});
            skLineSegment(sketch, "E28.2.13.0", {"start": v(-28.08, -15.37) * mm, "end": v(-26.11, -14.77) * mm});
            skLineSegment(sketch, "E28.3.13.0", {"start": v(-28.51, -14.53) * mm, "end": v(-28.08, -15.37) * mm});
            skLineSegment(sketch, "E28.6.13.0", {"start": v(-28.51, -14.53) * mm, "end": v(-28.94, -13.69) * mm});
            skLineSegment(sketch, "E28.9.13.0", {"start": v(-28.94, -13.69) * mm, "end": v(-27.3, -12.45) * mm});
            skLineSegment(sketch, "E28.2.14.0", {"start": v(-25.33, -19.57) * mm, "end": v(-23.48, -18.67) * mm});
            skLineSegment(sketch, "E28.3.14.0", {"start": v(-25.89, -18.8) * mm, "end": v(-25.33, -19.57) * mm});
            skLineSegment(sketch, "E28.6.14.0", {"start": v(-25.89, -18.8) * mm, "end": v(-26.44, -18.05) * mm});
            skLineSegment(sketch, "E28.9.14.0", {"start": v(-26.44, -18.05) * mm, "end": v(-25.01, -16.57) * mm});
            skLineSegment(sketch, "E28.2.15.0", {"start": v(-21.96, -23.3) * mm, "end": v(-20.27, -22.11) * mm});
            skLineSegment(sketch, "E28.3.15.0", {"start": v(-22.63, -22.63) * mm, "end": v(-21.96, -23.3) * mm});
            skLineSegment(sketch, "E28.6.15.0", {"start": v(-22.63, -22.63) * mm, "end": v(-23.3, -21.96) * mm});
            skLineSegment(sketch, "E28.9.15.0", {"start": v(-23.3, -21.96) * mm, "end": v(-22.11, -20.27) * mm});
            skLineSegment(sketch, "E28.2.16.0", {"start": v(-18.05, -26.44) * mm, "end": v(-16.57, -25.01) * mm});
            skLineSegment(sketch, "E28.3.16.0", {"start": v(-18.8, -25.89) * mm, "end": v(-18.05, -26.44) * mm});
            skLineSegment(sketch, "E28.6.16.0", {"start": v(-18.8, -25.89) * mm, "end": v(-19.57, -25.33) * mm});
            skLineSegment(sketch, "E28.9.16.0", {"start": v(-19.57, -25.33) * mm, "end": v(-18.67, -23.48) * mm});
            skLineSegment(sketch, "E28.2.17.0", {"start": v(-13.69, -28.94) * mm, "end": v(-12.45, -27.3) * mm});
            skLineSegment(sketch, "E28.3.17.0", {"start": v(-14.53, -28.51) * mm, "end": v(-13.69, -28.94) * mm});
            skLineSegment(sketch, "E28.6.17.0", {"start": v(-14.53, -28.51) * mm, "end": v(-15.37, -28.08) * mm});
            skLineSegment(sketch, "E28.9.17.0", {"start": v(-15.37, -28.08) * mm, "end": v(-14.77, -26.11) * mm});
            skLineSegment(sketch, "E28.2.18.0", {"start": v(-9, -30.73) * mm, "end": v(-8.03, -28.9) * mm});
            skLineSegment(sketch, "E28.3.18.0", {"start": v(-9.89, -30.43) * mm, "end": v(-9, -30.73) * mm});
            skLineSegment(sketch, "E28.6.18.0", {"start": v(-9.89, -30.43) * mm, "end": v(-10.78, -30.14) * mm});
            skLineSegment(sketch, "E28.9.18.0", {"start": v(-10.78, -30.14) * mm, "end": v(-10.5, -28.1) * mm});
            skLineSegment(sketch, "E28.2.19.0", {"start": v(-4.08, -31.75) * mm, "end": v(-3.4, -29.8) * mm});
            skLineSegment(sketch, "E28.3.19.0", {"start": v(-5, -31.6) * mm, "end": v(-4.08, -31.75) * mm});
            skLineSegment(sketch, "E28.6.19.0", {"start": v(-5, -31.6) * mm, "end": v(-5.94, -31.46) * mm});
            skLineSegment(sketch, "E28.9.19.0", {"start": v(-5.94, -31.46) * mm, "end": v(-5.97, -29.4) * mm});
            skLineSegment(sketch, "E28.2.20.0", {"start": v(0.94, -32) * mm, "end": v(1.3, -29.97) * mm});
            skLineSegment(sketch, "E28.3.20.0", {"start": v(0, -32) * mm, "end": v(0.94, -32) * mm});
            skLineSegment(sketch, "E28.6.20.0", {"start": v(0, -32) * mm, "end": v(-0.94, -32) * mm});
            skLineSegment(sketch, "E28.9.20.0", {"start": v(-0.94, -32) * mm, "end": v(-1.3, -29.97) * mm});
            skLineSegment(sketch, "E28.2.21.0", {"start": v(5.94, -31.46) * mm, "end": v(5.97, -29.4) * mm});
            skLineSegment(sketch, "E28.3.21.0", {"start": v(5, -31.6) * mm, "end": v(5.94, -31.46) * mm});
            skLineSegment(sketch, "E28.6.21.0", {"start": v(5, -31.6) * mm, "end": v(4.08, -31.75) * mm});
            skLineSegment(sketch, "E28.9.21.0", {"start": v(4.08, -31.75) * mm, "end": v(3.4, -29.8) * mm});
            skLineSegment(sketch, "E28.2.22.0", {"start": v(10.78, -30.14) * mm, "end": v(10.5, -28.1) * mm});
            skLineSegment(sketch, "E28.3.22.0", {"start": v(9.89, -30.43) * mm, "end": v(10.78, -30.14) * mm});
            skLineSegment(sketch, "E28.6.22.0", {"start": v(9.89, -30.43) * mm, "end": v(9, -30.73) * mm});
            skLineSegment(sketch, "E28.9.22.0", {"start": v(9, -30.73) * mm, "end": v(8.03, -28.9) * mm});
            skLineSegment(sketch, "E28.2.23.0", {"start": v(15.37, -28.08) * mm, "end": v(14.77, -26.11) * mm});
            skLineSegment(sketch, "E28.3.23.0", {"start": v(14.53, -28.51) * mm, "end": v(15.37, -28.08) * mm});
            skLineSegment(sketch, "E28.6.23.0", {"start": v(14.53, -28.51) * mm, "end": v(13.69, -28.94) * mm});
            skLineSegment(sketch, "E28.9.23.0", {"start": v(13.69, -28.94) * mm, "end": v(12.45, -27.3) * mm});
            skLineSegment(sketch, "E28.2.24.0", {"start": v(19.57, -25.33) * mm, "end": v(18.67, -23.48) * mm});
            skLineSegment(sketch, "E28.3.24.0", {"start": v(18.8, -25.89) * mm, "end": v(19.57, -25.33) * mm});
            skLineSegment(sketch, "E28.6.24.0", {"start": v(18.8, -25.89) * mm, "end": v(18.05, -26.44) * mm});
            skLineSegment(sketch, "E28.9.24.0", {"start": v(18.05, -26.44) * mm, "end": v(16.57, -25.01) * mm});
            skLineSegment(sketch, "E28.2.25.0", {"start": v(23.3, -21.96) * mm, "end": v(22.11, -20.27) * mm});
            skLineSegment(sketch, "E28.3.25.0", {"start": v(22.63, -22.63) * mm, "end": v(23.3, -21.96) * mm});
            skLineSegment(sketch, "E28.6.25.0", {"start": v(22.63, -22.63) * mm, "end": v(21.96, -23.3) * mm});
            skLineSegment(sketch, "E28.9.25.0", {"start": v(21.96, -23.3) * mm, "end": v(20.27, -22.11) * mm});
            skLineSegment(sketch, "E28.2.26.0", {"start": v(26.44, -18.05) * mm, "end": v(25.01, -16.57) * mm});
            skLineSegment(sketch, "E28.3.26.0", {"start": v(25.89, -18.8) * mm, "end": v(26.44, -18.05) * mm});
            skLineSegment(sketch, "E28.6.26.0", {"start": v(25.89, -18.8) * mm, "end": v(25.33, -19.57) * mm});
            skLineSegment(sketch, "E28.9.26.0", {"start": v(25.33, -19.57) * mm, "end": v(23.48, -18.67) * mm});
            skLineSegment(sketch, "E28.2.27.0", {"start": v(28.94, -13.69) * mm, "end": v(27.3, -12.45) * mm});
            skLineSegment(sketch, "E28.3.27.0", {"start": v(28.51, -14.53) * mm, "end": v(28.94, -13.69) * mm});
            skLineSegment(sketch, "E28.6.27.0", {"start": v(28.51, -14.53) * mm, "end": v(28.08, -15.37) * mm});
            skLineSegment(sketch, "E28.9.27.0", {"start": v(28.08, -15.37) * mm, "end": v(26.11, -14.77) * mm});
            skLineSegment(sketch, "E28.2.28.0", {"start": v(30.73, -9) * mm, "end": v(28.9, -8.03) * mm});
            skLineSegment(sketch, "E28.3.28.0", {"start": v(30.43, -9.89) * mm, "end": v(30.73, -9) * mm});
            skLineSegment(sketch, "E28.6.28.0", {"start": v(30.43, -9.89) * mm, "end": v(30.14, -10.78) * mm});
            skLineSegment(sketch, "E28.9.28.0", {"start": v(30.14, -10.78) * mm, "end": v(28.1, -10.5) * mm});
            skLineSegment(sketch, "E28.2.29.0", {"start": v(31.75, -4.08) * mm, "end": v(29.8, -3.4) * mm});
            skLineSegment(sketch, "E28.3.29.0", {"start": v(31.6, -5) * mm, "end": v(31.75, -4.08) * mm});
            skLineSegment(sketch, "E28.6.29.0", {"start": v(31.6, -5) * mm, "end": v(31.46, -5.94) * mm});
            skLineSegment(sketch, "E28.9.29.0", {"start": v(31.46, -5.94) * mm, "end": v(29.4, -5.97) * mm});
            skLineSegment(sketch, "E28.2.30.0", {"start": v(32, 0.94) * mm, "end": v(29.97, 1.3) * mm});
            skLineSegment(sketch, "E28.3.30.0", {"start": v(32, 0) * mm, "end": v(32, 0.94) * mm});
            skLineSegment(sketch, "E28.6.30.0", {"start": v(32, 0) * mm, "end": v(32, -0.94) * mm});
            skLineSegment(sketch, "E28.9.30.0", {"start": v(32, -0.94) * mm, "end": v(29.97, -1.3) * mm});
            skLineSegment(sketch, "E28.2.31.0", {"start": v(31.46, 5.94) * mm, "end": v(29.4, 5.97) * mm});
            skLineSegment(sketch, "E28.3.31.0", {"start": v(31.6, 5) * mm, "end": v(31.46, 5.94) * mm});
            skLineSegment(sketch, "E28.6.31.0", {"start": v(31.6, 5) * mm, "end": v(31.75, 4.08) * mm});
            skLineSegment(sketch, "E28.9.31.0", {"start": v(31.75, 4.08) * mm, "end": v(29.8, 3.4) * mm});
            skLineSegment(sketch, "E28.2.32.0", {"start": v(30.14, 10.78) * mm, "end": v(28.1, 10.5) * mm});
            skLineSegment(sketch, "E28.3.32.0", {"start": v(30.43, 9.89) * mm, "end": v(30.14, 10.78) * mm});
            skLineSegment(sketch, "E28.6.32.0", {"start": v(30.43, 9.89) * mm, "end": v(30.73, 9) * mm});
            skLineSegment(sketch, "E28.9.32.0", {"start": v(30.73, 9) * mm, "end": v(28.9, 8.03) * mm});
            skLineSegment(sketch, "E28.2.33.0", {"start": v(28.08, 15.37) * mm, "end": v(26.11, 14.77) * mm});
            skLineSegment(sketch, "E28.3.33.0", {"start": v(28.51, 14.53) * mm, "end": v(28.08, 15.37) * mm});
            skLineSegment(sketch, "E28.6.33.0", {"start": v(28.51, 14.53) * mm, "end": v(28.94, 13.69) * mm});
            skLineSegment(sketch, "E28.9.33.0", {"start": v(28.94, 13.69) * mm, "end": v(27.3, 12.45) * mm});
            skLineSegment(sketch, "E28.2.34.0", {"start": v(25.33, 19.57) * mm, "end": v(23.48, 18.67) * mm});
            skLineSegment(sketch, "E28.3.34.0", {"start": v(25.89, 18.8) * mm, "end": v(25.33, 19.57) * mm});
            skLineSegment(sketch, "E28.6.34.0", {"start": v(25.89, 18.8) * mm, "end": v(26.44, 18.05) * mm});
            skLineSegment(sketch, "E28.9.34.0", {"start": v(26.44, 18.05) * mm, "end": v(25.01, 16.57) * mm});
            skLineSegment(sketch, "E28.2.35.0", {"start": v(21.96, 23.3) * mm, "end": v(20.27, 22.11) * mm});
            skLineSegment(sketch, "E28.3.35.0", {"start": v(22.63, 22.63) * mm, "end": v(21.96, 23.3) * mm});
            skLineSegment(sketch, "E28.6.35.0", {"start": v(22.63, 22.63) * mm, "end": v(23.3, 21.96) * mm});
            skLineSegment(sketch, "E28.9.35.0", {"start": v(23.3, 21.96) * mm, "end": v(22.11, 20.27) * mm});
            skLineSegment(sketch, "E28.2.36.0", {"start": v(18.05, 26.44) * mm, "end": v(16.57, 25.01) * mm});
            skLineSegment(sketch, "E28.3.36.0", {"start": v(18.8, 25.89) * mm, "end": v(18.05, 26.44) * mm});
            skLineSegment(sketch, "E28.6.36.0", {"start": v(18.8, 25.89) * mm, "end": v(19.57, 25.33) * mm});
            skLineSegment(sketch, "E28.9.36.0", {"start": v(19.57, 25.33) * mm, "end": v(18.67, 23.48) * mm});
            skLineSegment(sketch, "E28.2.37.0", {"start": v(13.69, 28.94) * mm, "end": v(12.45, 27.3) * mm});
            skLineSegment(sketch, "E28.3.37.0", {"start": v(14.53, 28.51) * mm, "end": v(13.69, 28.94) * mm});
            skLineSegment(sketch, "E28.6.37.0", {"start": v(14.53, 28.51) * mm, "end": v(15.37, 28.08) * mm});
            skLineSegment(sketch, "E28.9.37.0", {"start": v(15.37, 28.08) * mm, "end": v(14.77, 26.11) * mm});
            skLineSegment(sketch, "E28.2.38.0", {"start": v(9, 30.73) * mm, "end": v(8.03, 28.9) * mm});
            skLineSegment(sketch, "E28.3.38.0", {"start": v(9.89, 30.43) * mm, "end": v(9, 30.73) * mm});
            skLineSegment(sketch, "E28.6.38.0", {"start": v(9.89, 30.43) * mm, "end": v(10.78, 30.14) * mm});
            skLineSegment(sketch, "E28.9.38.0", {"start": v(10.78, 30.14) * mm, "end": v(10.5, 28.1) * mm});
            skLineSegment(sketch, "E28.2.39.0", {"start": v(4.08, 31.75) * mm, "end": v(3.4, 29.8) * mm});
            skLineSegment(sketch, "E28.3.39.0", {"start": v(5, 31.6) * mm, "end": v(4.08, 31.75) * mm});
            skLineSegment(sketch, "E28.6.39.0", {"start": v(5, 31.6) * mm, "end": v(5.94, 31.46) * mm});
            skLineSegment(sketch, "E28.9.39.0", {"start": v(5.94, 31.46) * mm, "end": v(5.97, 29.4) * mm});
            skSolve(sketch);
        }
        {
            var Q0;
            Q0 = qSketchRegion(id + "F14", true);
            extrude(context, id + "F15", {"entities" : qUnion([Q0]), "operationType" : NewBodyOperationType.ADD, "depth" : 4 * mm, "offsetDistance" : 25 * mm});
        }
        {
            var Q0;
            Q0=makeQuery(id+"F7.opExtrude","CAP_FACE",FACE,{"disambiguationData":[OSD([sQuery(id+"F0.wireOp",EDGE,"E0")])],"isStart":false});
            var sketch = newSketch(context, id + "F16", { "sketchPlane" : qUnion([Q0])});
            skCircle(sketch, "E29", {"center": v(40, 0) * mm, "radius": 7.5 * mm});
            skLineSegment(sketch, "E30", {"start": v(40, 0) * mm, "end": v(40, 7.5) * mm, "construction": true});
            skLineSegment(sketch, "E31", {"start": v(38.68, 7.38) * mm, "end": v(39.06, 9.5) * mm});
            skLineSegment(sketch, "E32", {"start": v(39.06, 9.5) * mm, "end": v(40.94, 9.5) * mm});
            skLineSegment(sketch, "E33.MirrorCS", {"start": v(41.32, 7.38) * mm, "end": v(40.94, 9.5) * mm});
            skLineSegment(sketch, "E34.1.0", {"start": v(34.6, 5.2) * mm, "end": v(33.65, 7.13) * mm});
            skLineSegment(sketch, "E34.1.1", {"start": v(33.65, 7.13) * mm, "end": v(35.18, 8.24) * mm});
            skLineSegment(sketch, "E34.1.2", {"start": v(36.72, 6.75) * mm, "end": v(35.18, 8.24) * mm});
            skLineSegment(sketch, "E34.2.0", {"start": v(32.57, 1.03) * mm, "end": v(30.67, 2.04) * mm});
            skLineSegment(sketch, "E34.2.1", {"start": v(30.67, 2.04) * mm, "end": v(31.26, 3.83) * mm});
            skLineSegment(sketch, "E34.2.2", {"start": v(33.38, 3.53) * mm, "end": v(31.26, 3.83) * mm});
            skLineSegment(sketch, "E35.1.3.0", {"start": v(33.38, -3.53) * mm, "end": v(31.26, -3.83) * mm});
            skLineSegment(sketch, "E35.3.3.0", {"start": v(31.26, -3.83) * mm, "end": v(30.67, -2.04) * mm});
            skLineSegment(sketch, "E35.6.3.0", {"start": v(32.57, -1.03) * mm, "end": v(30.67, -2.04) * mm});
            skLineSegment(sketch, "E35.1.4.0", {"start": v(36.72, -6.75) * mm, "end": v(35.18, -8.24) * mm});
            skLineSegment(sketch, "E35.3.4.0", {"start": v(35.18, -8.24) * mm, "end": v(33.65, -7.13) * mm});
            skLineSegment(sketch, "E35.6.4.0", {"start": v(34.6, -5.2) * mm, "end": v(33.65, -7.13) * mm});
            skLineSegment(sketch, "E35.1.5.0", {"start": v(41.32, -7.38) * mm, "end": v(40.94, -9.5) * mm});
            skLineSegment(sketch, "E35.3.5.0", {"start": v(40.94, -9.5) * mm, "end": v(39.06, -9.5) * mm});
            skLineSegment(sketch, "E35.6.5.0", {"start": v(38.68, -7.38) * mm, "end": v(39.06, -9.5) * mm});
            skLineSegment(sketch, "E35.1.6.0", {"start": v(45.4, -5.2) * mm, "end": v(46.35, -7.13) * mm});
            skLineSegment(sketch, "E35.3.6.0", {"start": v(46.35, -7.13) * mm, "end": v(44.82, -8.24) * mm});
            skLineSegment(sketch, "E35.6.6.0", {"start": v(43.28, -6.75) * mm, "end": v(44.82, -8.24) * mm});
            skLineSegment(sketch, "E35.1.7.0", {"start": v(47.43, -1.03) * mm, "end": v(49.33, -2.04) * mm});
            skLineSegment(sketch, "E35.3.7.0", {"start": v(49.33, -2.04) * mm, "end": v(48.74, -3.83) * mm});
            skLineSegment(sketch, "E35.6.7.0", {"start": v(46.62, -3.53) * mm, "end": v(48.74, -3.83) * mm});
            skLineSegment(sketch, "E35.1.8.0", {"start": v(46.62, 3.53) * mm, "end": v(48.74, 3.83) * mm});
            skLineSegment(sketch, "E35.3.8.0", {"start": v(48.74, 3.83) * mm, "end": v(49.33, 2.04) * mm});
            skLineSegment(sketch, "E35.6.8.0", {"start": v(47.43, 1.03) * mm, "end": v(49.33, 2.04) * mm});
            skLineSegment(sketch, "E35.1.9.0", {"start": v(43.28, 6.75) * mm, "end": v(44.82, 8.24) * mm});
            skLineSegment(sketch, "E35.3.9.0", {"start": v(44.82, 8.24) * mm, "end": v(46.35, 7.13) * mm});
            skLineSegment(sketch, "E35.6.9.0", {"start": v(45.4, 5.2) * mm, "end": v(46.35, 7.13) * mm});
            skSolve(sketch);
        }
        {
            var Q0;
            Q0 = qSketchRegion(id + "F16", true);
            extrude(context, id + "F17", {"entities" : qUnion([Q0]), "operationType" : NewBodyOperationType.ADD, "depth" : 4 * mm, "offsetDistance" : 25 * mm});
        }
        {
            var Q0;
            Q0=makeQuery(id+"F17.opExtrude","CAP_FACE",FACE,{"disambiguationData":[OSD([sQuery(id+"F16.wireOp",EDGE,"E29"),sQuery(id+"F16.wireOp",EDGE,"E31"),sQuery(id+"F16.wireOp",EDGE,"E32"),sQuery(id+"F16.wireOp",EDGE,"E33.MirrorCS"),sQuery(id+"F16.wireOp",EDGE,"E34.1.0"),sQuery(id+"F16.wireOp",EDGE,"E34.1.1"),sQuery(id+"F16.wireOp",EDGE,"E34.1.2"),sQuery(id+"F16.wireOp",EDGE,"E34.2.0"),sQuery(id+"F16.wireOp",EDGE,"E34.2.1"),sQuery(id+"F16.wireOp",EDGE,"E34.2.2"),sQuery(id+"F16.wireOp",EDGE,"E35.1.3.0"),sQuery(id+"F16.wireOp",EDGE,"E35.3.3.0"),sQuery(id+"F16.wireOp",EDGE,"E35.6.3.0"),sQuery(id+"F16.wireOp",EDGE,"E35.1.4.0"),sQuery(id+"F16.wireOp",EDGE,"E35.3.4.0"),sQuery(id+"F16.wireOp",EDGE,"E35.6.4.0"),sQuery(id+"F16.wireOp",EDGE,"E35.1.5.0"),sQuery(id+"F16.wireOp",EDGE,"E35.3.5.0"),sQuery(id+"F16.wireOp",EDGE,"E35.6.5.0"),sQuery(id+"F16.wireOp",EDGE,"E35.1.6.0"),sQuery(id+"F16.wireOp",EDGE,"E35.3.6.0"),sQuery(id+"F16.wireOp",EDGE,"E35.6.6.0"),sQuery(id+"F16.wireOp",EDGE,"E35.1.7.0"),sQuery(id+"F16.wireOp",EDGE,"E35.3.7.0"),sQuery(id+"F16.wireOp",EDGE,"E35.6.7.0"),sQuery(id+"F16.wireOp",EDGE,"E35.1.8.0"),sQuery(id+"F16.wireOp",EDGE,"E35.3.8.0"),sQuery(id+"F16.wireOp",EDGE,"E35.6.8.0"),sQuery(id+"F16.wireOp",EDGE,"E35.1.9.0"),sQuery(id+"F16.wireOp",EDGE,"E35.3.9.0"),sQuery(id+"F16.wireOp",EDGE,"E35.6.9.0")])],"isStart":false});
            var sketch = newSketch(context, id + "F18", { "sketchPlane" : qUnion([Q0])});
            skCircle(sketch, "E36.0", {"center": v(40, 0) * mm, "radius": 3 * mm});
            skSolve(sketch);
        }
        {
            var Q0;
            Q0 = qSketchRegion(id + "F18", true);
            extrude(context, id + "F19", {"entities" : qUnion([Q0]), "operationType" : NewBodyOperationType.ADD, "depth" : 2 * mm, "offsetDistance" : 25 * mm});
        }
        {
            var Q0;
            Q0=makeQuery(id+"F19.opExtrude","CAP_FACE",FACE,{"disambiguationData":[OSD([sQuery(id+"F18.wireOp",EDGE,"E36.0")])],"isStart":false});
            var sketch = newSketch(context, id + "F20", { "sketchPlane" : qUnion([Q0])});
            skCircle(sketch, "E37", {"center": v(0, 0) * mm, "radius": 98 * mm});
            skCircle(sketch, "E38.0", {"center": v(0, 0) * mm, "radius": 5 * mm});
            skSolve(sketch);
        }
        {
            var Q0;
            Q0 = qSketchRegion(id + "F20", true);
            extrude(context, id + "F21", {"entities" : qUnion([Q0]), "depth" : 1 * mm, "offsetDistance" : 25 * mm});
        }
        {
            var Q0;
            Q0=makeQuery(id+"F21.opExtrude","SWEPT_BODY",BODY,{"disambiguationData":[OSD([sQuery(id+"F20.wireOp",EDGE,"E37"),sQuery(id+"F20.wireOp",EDGE,"E38.0")])]});
            var Q1;
            Q1=makeQuery(id+"F1.opExtrude","SWEPT_BODY",BODY,{"disambiguationData":[OSD([sQuery(id+"F0.wireOp",EDGE,"E0")])]});
            booleanBodies(context, id + "F22", {"operationType" : BooleanOperationType.SUBTRACTION, "tools" : qUnion([Q0]), "targets" : qUnion([Q1]), "keepTools" : true});
        }
        {
            var Q0;
            Q0=makeQuery(id+"F21.opExtrude","CAP_FACE",FACE,{"disambiguationData":[OSD([sQuery(id+"F20.wireOp",EDGE,"E37"),sQuery(id+"F20.wireOp",EDGE,"E38.0")])],"isStart":true});
            var sketch = newSketch(context, id + "F23", { "sketchPlane" : qUnion([Q0])});
            skCircle(sketch, "E39.0", {"center": v(-40, 0) * mm, "radius": 3 * mm});
            skCircle(sketch, "E40", {"center": v(-40, 0) * mm, "radius": 5 * mm});
            skSolve(sketch);
        }
        {
            var Q0;
            Q0 = qSketchRegion(id + "F23", true);
            extrude(context, id + "F24", {"entities" : qUnion([Q0]), "operationType" : NewBodyOperationType.ADD, "endBound" : BoundingType.UP_TO_NEXT, "depth" : 25 * mm, "offsetDistance" : 25 * mm});
        }
        {
            var Q0;
            Q0=makeQuery(id+"F21.opExtrude","CAP_FACE",FACE,{"disambiguationData":[OSD([sQuery(id+"F20.wireOp",EDGE,"E37"),sQuery(id+"F20.wireOp",EDGE,"E38.0")])],"isStart":false});
            var sketch = newSketch(context, id + "F25", { "sketchPlane" : qUnion([Q0])});
            skLineSegment(sketch, "E41.bottom", {"start": v(1.5, 91) * mm, "end": v(-1.5, 91) * mm});
            skLineSegment(sketch, "E41.top", {"start": v(1.5, 71) * mm, "end": v(-1.5, 71) * mm});
            skLineSegment(sketch, "E41.left", {"start": v(1.5, 91) * mm, "end": v(1.5, 71) * mm});
            skLineSegment(sketch, "E41.right", {"start": v(-1.5, 91) * mm, "end": v(-1.5, 71) * mm});
            skPoint(sketch, "E41.middle", {"position": v(0, 81) * mm});
            skLineSegment(sketch, "E42.1.0", {"start": v(-46.8, 78.06) * mm, "end": v(-36.8, 60.74) * mm});
            skLineSegment(sketch, "E42.1.1", {"start": v(-44.2, 79.56) * mm, "end": v(-46.8, 78.06) * mm});
            skLineSegment(sketch, "E42.1.2", {"start": v(-44.2, 79.56) * mm, "end": v(-34.2, 62.24) * mm});
            skLineSegment(sketch, "E42.1.3", {"start": v(-34.2, 62.24) * mm, "end": v(-36.8, 60.74) * mm});
            skLineSegment(sketch, "E42.2.0", {"start": v(-79.56, 44.2) * mm, "end": v(-62.24, 34.2) * mm});
            skLineSegment(sketch, "E42.2.1", {"start": v(-78.06, 46.8) * mm, "end": v(-79.56, 44.2) * mm});
            skLineSegment(sketch, "E42.2.2", {"start": v(-78.06, 46.8) * mm, "end": v(-60.74, 36.8) * mm});
            skLineSegment(sketch, "E42.2.3", {"start": v(-60.74, 36.8) * mm, "end": v(-62.24, 34.2) * mm});
            skPoint(sketch, "E42.center", {"position": v(0, 0) * mm});
            skLineSegment(sketch, "E43.2.3.0", {"start": v(-91, -1.5) * mm, "end": v(-71, -1.5) * mm});
            skLineSegment(sketch, "E43.3.3.0", {"start": v(-91, 1.5) * mm, "end": v(-91, -1.5) * mm});
            skLineSegment(sketch, "E43.6.3.0", {"start": v(-91, 1.5) * mm, "end": v(-71, 1.5) * mm});
            skLineSegment(sketch, "E43.9.3.0", {"start": v(-71, 1.5) * mm, "end": v(-71, -1.5) * mm});
            skLineSegment(sketch, "E43.2.4.0", {"start": v(-78.06, -46.8) * mm, "end": v(-60.74, -36.8) * mm});
            skLineSegment(sketch, "E43.3.4.0", {"start": v(-79.56, -44.2) * mm, "end": v(-78.06, -46.8) * mm});
            skLineSegment(sketch, "E43.6.4.0", {"start": v(-79.56, -44.2) * mm, "end": v(-62.24, -34.2) * mm});
            skLineSegment(sketch, "E43.9.4.0", {"start": v(-62.24, -34.2) * mm, "end": v(-60.74, -36.8) * mm});
            skLineSegment(sketch, "E43.2.5.0", {"start": v(-44.2, -79.56) * mm, "end": v(-34.2, -62.24) * mm});
            skLineSegment(sketch, "E43.3.5.0", {"start": v(-46.8, -78.06) * mm, "end": v(-44.2, -79.56) * mm});
            skLineSegment(sketch, "E43.6.5.0", {"start": v(-46.8, -78.06) * mm, "end": v(-36.8, -60.74) * mm});
            skLineSegment(sketch, "E43.9.5.0", {"start": v(-36.8, -60.74) * mm, "end": v(-34.2, -62.24) * mm});
            skLineSegment(sketch, "E43.2.6.0", {"start": v(1.5, -91) * mm, "end": v(1.5, -71) * mm});
            skLineSegment(sketch, "E43.3.6.0", {"start": v(-1.5, -91) * mm, "end": v(1.5, -91) * mm});
            skLineSegment(sketch, "E43.6.6.0", {"start": v(-1.5, -91) * mm, "end": v(-1.5, -71) * mm});
            skLineSegment(sketch, "E43.9.6.0", {"start": v(-1.5, -71) * mm, "end": v(1.5, -71) * mm});
            skLineSegment(sketch, "E43.2.7.0", {"start": v(46.8, -78.06) * mm, "end": v(36.8, -60.74) * mm});
            skLineSegment(sketch, "E43.3.7.0", {"start": v(44.2, -79.56) * mm, "end": v(46.8, -78.06) * mm});
            skLineSegment(sketch, "E43.6.7.0", {"start": v(44.2, -79.56) * mm, "end": v(34.2, -62.24) * mm});
            skLineSegment(sketch, "E43.9.7.0", {"start": v(34.2, -62.24) * mm, "end": v(36.8, -60.74) * mm});
            skLineSegment(sketch, "E43.2.8.0", {"start": v(79.56, -44.2) * mm, "end": v(62.24, -34.2) * mm});
            skLineSegment(sketch, "E43.3.8.0", {"start": v(78.06, -46.8) * mm, "end": v(79.56, -44.2) * mm});
            skLineSegment(sketch, "E43.6.8.0", {"start": v(78.06, -46.8) * mm, "end": v(60.74, -36.8) * mm});
            skLineSegment(sketch, "E43.9.8.0", {"start": v(60.74, -36.8) * mm, "end": v(62.24, -34.2) * mm});
            skLineSegment(sketch, "E43.2.9.0", {"start": v(91, 1.5) * mm, "end": v(71, 1.5) * mm});
            skLineSegment(sketch, "E43.3.9.0", {"start": v(91, -1.5) * mm, "end": v(91, 1.5) * mm});
            skLineSegment(sketch, "E43.6.9.0", {"start": v(91, -1.5) * mm, "end": v(71, -1.5) * mm});
            skLineSegment(sketch, "E43.9.9.0", {"start": v(71, -1.5) * mm, "end": v(71, 1.5) * mm});
            skLineSegment(sketch, "E43.2.10.0", {"start": v(78.06, 46.8) * mm, "end": v(60.74, 36.8) * mm});
            skLineSegment(sketch, "E43.3.10.0", {"start": v(79.56, 44.2) * mm, "end": v(78.06, 46.8) * mm});
            skLineSegment(sketch, "E43.6.10.0", {"start": v(79.56, 44.2) * mm, "end": v(62.24, 34.2) * mm});
            skLineSegment(sketch, "E43.9.10.0", {"start": v(62.24, 34.2) * mm, "end": v(60.74, 36.8) * mm});
            skLineSegment(sketch, "E43.2.11.0", {"start": v(44.2, 79.56) * mm, "end": v(34.2, 62.24) * mm});
            skLineSegment(sketch, "E43.3.11.0", {"start": v(46.8, 78.06) * mm, "end": v(44.2, 79.56) * mm});
            skLineSegment(sketch, "E43.6.11.0", {"start": v(46.8, 78.06) * mm, "end": v(36.8, 60.74) * mm});
            skLineSegment(sketch, "E43.9.11.0", {"start": v(36.8, 60.74) * mm, "end": v(34.2, 62.24) * mm});
            skSolve(sketch);
        }
        {
            var Q0;
            Q0 = qSketchRegion(id + "F25", true);
            extrude(context, id + "F26", {"entities" : qUnion([Q0]), "operationType" : NewBodyOperationType.REMOVE, "oppositeDirection" : true, "depth" : 0.5 * mm, "offsetDistance" : 25 * mm});
        }
        {
            var Q0;
            Q0=makeQuery(id+"F21.opExtrude","CAP_FACE",FACE,{"disambiguationData":[OSD([sQuery(id+"F20.wireOp",EDGE,"E37"),sQuery(id+"F20.wireOp",EDGE,"E38.0")])],"isStart":false});
            var sketch = newSketch(context, id + "F27", { "sketchPlane" : qUnion([Q0])});
            skLineSegment(sketch, "E44.bottom", {"start": v(0.75, 90.5) * mm, "end": v(-0.75, 90.5) * mm});
            skLineSegment(sketch, "E44.top", {"start": v(0.75, 78.5) * mm, "end": v(-0.75, 78.5) * mm});
            skLineSegment(sketch, "E44.left", {"start": v(0.75, 90.5) * mm, "end": v(0.75, 78.5) * mm});
            skLineSegment(sketch, "E44.right", {"start": v(-0.75, 90.5) * mm, "end": v(-0.75, 78.5) * mm});
            skPoint(sketch, "E44.middle", {"position": v(0, 84.5) * mm});
            skLineSegment(sketch, "E45.1.0", {"start": v(-10.2, 89.93) * mm, "end": v(-8.95, 78) * mm});
            skLineSegment(sketch, "E45.1.1", {"start": v(-8.71, 90.08) * mm, "end": v(-10.2, 89.93) * mm});
            skLineSegment(sketch, "E45.1.2", {"start": v(-8.71, 90.08) * mm, "end": v(-7.46, 78.15) * mm});
            skLineSegment(sketch, "E45.1.3", {"start": v(-7.46, 78.15) * mm, "end": v(-8.95, 78) * mm});
            skLineSegment(sketch, "E45.2.0", {"start": v(-19.55, 88.37) * mm, "end": v(-17.05, 76.63) * mm});
            skLineSegment(sketch, "E45.2.1", {"start": v(-18.08, 88.68) * mm, "end": v(-19.55, 88.37) * mm});
            skLineSegment(sketch, "E45.2.2", {"start": v(-18.08, 88.68) * mm, "end": v(-15.59, 76.94) * mm});
            skLineSegment(sketch, "E45.2.3", {"start": v(-15.59, 76.94) * mm, "end": v(-17.05, 76.63) * mm});
            skPoint(sketch, "E45.center", {"position": v(0, 0) * mm});
            skLineSegment(sketch, "E46.2.3.0", {"start": v(-28.68, 85.84) * mm, "end": v(-24.97, 74.43) * mm});
            skLineSegment(sketch, "E46.3.3.0", {"start": v(-27.25, 86.3) * mm, "end": v(-28.68, 85.84) * mm});
            skLineSegment(sketch, "E46.6.3.0", {"start": v(-27.25, 86.3) * mm, "end": v(-23.54, 74.89) * mm});
            skLineSegment(sketch, "E46.9.3.0", {"start": v(-23.54, 74.89) * mm, "end": v(-24.97, 74.43) * mm});
            skLineSegment(sketch, "E46.2.4.0", {"start": v(-37.5, 82.37) * mm, "end": v(-32.61, 71.4) * mm});
            skLineSegment(sketch, "E46.3.4.0", {"start": v(-36.12, 82.98) * mm, "end": v(-37.5, 82.37) * mm});
            skLineSegment(sketch, "E46.6.4.0", {"start": v(-36.12, 82.98) * mm, "end": v(-31.24, 72.02) * mm});
            skLineSegment(sketch, "E46.9.4.0", {"start": v(-31.24, 72.02) * mm, "end": v(-32.61, 71.4) * mm});
            skLineSegment(sketch, "E46.2.5.0", {"start": v(-45.9, 78) * mm, "end": v(-39.9, 67.6) * mm});
            skLineSegment(sketch, "E46.3.5.0", {"start": v(-44.6, 78.75) * mm, "end": v(-45.9, 78) * mm});
            skLineSegment(sketch, "E46.6.5.0", {"start": v(-44.6, 78.75) * mm, "end": v(-38.6, 68.36) * mm});
            skLineSegment(sketch, "E46.9.5.0", {"start": v(-38.6, 68.36) * mm, "end": v(-39.9, 67.6) * mm});
            skLineSegment(sketch, "E46.2.6.0", {"start": v(-53.8, 72.78) * mm, "end": v(-46.75, 63.07) * mm});
            skLineSegment(sketch, "E46.3.6.0", {"start": v(-52.59, 73.66) * mm, "end": v(-53.8, 72.78) * mm});
            skLineSegment(sketch, "E46.6.6.0", {"start": v(-52.59, 73.66) * mm, "end": v(-45.53, 63.95) * mm});
            skLineSegment(sketch, "E46.9.6.0", {"start": v(-45.53, 63.95) * mm, "end": v(-46.75, 63.07) * mm});
            skLineSegment(sketch, "E46.2.7.0", {"start": v(-61.11, 66.75) * mm, "end": v(-53.08, 57.84) * mm});
            skLineSegment(sketch, "E46.3.7.0", {"start": v(-60, 67.76) * mm, "end": v(-61.11, 66.75) * mm});
            skLineSegment(sketch, "E46.6.7.0", {"start": v(-60, 67.76) * mm, "end": v(-51.97, 58.84) * mm});
            skLineSegment(sketch, "E46.9.7.0", {"start": v(-51.97, 58.84) * mm, "end": v(-53.08, 57.84) * mm});
            skLineSegment(sketch, "E46.2.8.0", {"start": v(-67.76, 60) * mm, "end": v(-58.84, 51.97) * mm});
            skLineSegment(sketch, "E46.3.8.0", {"start": v(-66.75, 61.11) * mm, "end": v(-67.76, 60) * mm});
            skLineSegment(sketch, "E46.6.8.0", {"start": v(-66.75, 61.11) * mm, "end": v(-57.84, 53.08) * mm});
            skLineSegment(sketch, "E46.9.8.0", {"start": v(-57.84, 53.08) * mm, "end": v(-58.84, 51.97) * mm});
            skLineSegment(sketch, "E46.2.9.0", {"start": v(-73.66, 52.59) * mm, "end": v(-63.95, 45.53) * mm});
            skLineSegment(sketch, "E46.3.9.0", {"start": v(-72.78, 53.8) * mm, "end": v(-73.66, 52.59) * mm});
            skLineSegment(sketch, "E46.6.9.0", {"start": v(-72.78, 53.8) * mm, "end": v(-63.07, 46.75) * mm});
            skLineSegment(sketch, "E46.9.9.0", {"start": v(-63.07, 46.75) * mm, "end": v(-63.95, 45.53) * mm});
            skLineSegment(sketch, "E46.2.10.0", {"start": v(-78.75, 44.6) * mm, "end": v(-68.36, 38.6) * mm});
            skLineSegment(sketch, "E46.3.10.0", {"start": v(-78, 45.9) * mm, "end": v(-78.75, 44.6) * mm});
            skLineSegment(sketch, "E46.6.10.0", {"start": v(-78, 45.9) * mm, "end": v(-67.6, 39.9) * mm});
            skLineSegment(sketch, "E46.9.10.0", {"start": v(-67.6, 39.9) * mm, "end": v(-68.36, 38.6) * mm});
            skLineSegment(sketch, "E46.2.11.0", {"start": v(-82.98, 36.12) * mm, "end": v(-72.02, 31.24) * mm});
            skLineSegment(sketch, "E46.3.11.0", {"start": v(-82.37, 37.5) * mm, "end": v(-82.98, 36.12) * mm});
            skLineSegment(sketch, "E46.6.11.0", {"start": v(-82.37, 37.5) * mm, "end": v(-71.4, 32.61) * mm});
            skLineSegment(sketch, "E46.9.11.0", {"start": v(-71.4, 32.61) * mm, "end": v(-72.02, 31.24) * mm});
            skLineSegment(sketch, "E46.2.12.0", {"start": v(-86.3, 27.25) * mm, "end": v(-74.89, 23.54) * mm});
            skLineSegment(sketch, "E46.3.12.0", {"start": v(-85.84, 28.68) * mm, "end": v(-86.3, 27.25) * mm});
            skLineSegment(sketch, "E46.6.12.0", {"start": v(-85.84, 28.68) * mm, "end": v(-74.43, 24.97) * mm});
            skLineSegment(sketch, "E46.9.12.0", {"start": v(-74.43, 24.97) * mm, "end": v(-74.89, 23.54) * mm});
            skLineSegment(sketch, "E46.2.13.0", {"start": v(-88.68, 18.08) * mm, "end": v(-76.94, 15.59) * mm});
            skLineSegment(sketch, "E46.3.13.0", {"start": v(-88.37, 19.55) * mm, "end": v(-88.68, 18.08) * mm});
            skLineSegment(sketch, "E46.6.13.0", {"start": v(-88.37, 19.55) * mm, "end": v(-76.63, 17.05) * mm});
            skLineSegment(sketch, "E46.9.13.0", {"start": v(-76.63, 17.05) * mm, "end": v(-76.94, 15.59) * mm});
            skLineSegment(sketch, "E46.2.14.0", {"start": v(-90.08, 8.71) * mm, "end": v(-78.15, 7.46) * mm});
            skLineSegment(sketch, "E46.3.14.0", {"start": v(-89.93, 10.2) * mm, "end": v(-90.08, 8.71) * mm});
            skLineSegment(sketch, "E46.6.14.0", {"start": v(-89.93, 10.2) * mm, "end": v(-78, 8.95) * mm});
            skLineSegment(sketch, "E46.9.14.0", {"start": v(-78, 8.95) * mm, "end": v(-78.15, 7.46) * mm});
            skLineSegment(sketch, "E46.2.15.0", {"start": v(-90.5, -0.75) * mm, "end": v(-78.5, -0.75) * mm});
            skLineSegment(sketch, "E46.3.15.0", {"start": v(-90.5, 0.75) * mm, "end": v(-90.5, -0.75) * mm});
            skLineSegment(sketch, "E46.6.15.0", {"start": v(-90.5, 0.75) * mm, "end": v(-78.5, 0.75) * mm});
            skLineSegment(sketch, "E46.9.15.0", {"start": v(-78.5, 0.75) * mm, "end": v(-78.5, -0.75) * mm});
            skLineSegment(sketch, "E46.2.16.0", {"start": v(-89.93, -10.2) * mm, "end": v(-78, -8.95) * mm});
            skLineSegment(sketch, "E46.3.16.0", {"start": v(-90.08, -8.71) * mm, "end": v(-89.93, -10.2) * mm});
            skLineSegment(sketch, "E46.6.16.0", {"start": v(-90.08, -8.71) * mm, "end": v(-78.15, -7.46) * mm});
            skLineSegment(sketch, "E46.9.16.0", {"start": v(-78.15, -7.46) * mm, "end": v(-78, -8.95) * mm});
            skLineSegment(sketch, "E46.2.17.0", {"start": v(-88.37, -19.55) * mm, "end": v(-76.63, -17.05) * mm});
            skLineSegment(sketch, "E46.3.17.0", {"start": v(-88.68, -18.08) * mm, "end": v(-88.37, -19.55) * mm});
            skLineSegment(sketch, "E46.6.17.0", {"start": v(-88.68, -18.08) * mm, "end": v(-76.94, -15.59) * mm});
            skLineSegment(sketch, "E46.9.17.0", {"start": v(-76.94, -15.59) * mm, "end": v(-76.63, -17.05) * mm});
            skLineSegment(sketch, "E46.2.18.0", {"start": v(-85.84, -28.68) * mm, "end": v(-74.43, -24.97) * mm});
            skLineSegment(sketch, "E46.3.18.0", {"start": v(-86.3, -27.25) * mm, "end": v(-85.84, -28.68) * mm});
            skLineSegment(sketch, "E46.6.18.0", {"start": v(-86.3, -27.25) * mm, "end": v(-74.89, -23.54) * mm});
            skLineSegment(sketch, "E46.9.18.0", {"start": v(-74.89, -23.54) * mm, "end": v(-74.43, -24.97) * mm});
            skLineSegment(sketch, "E46.2.19.0", {"start": v(-82.37, -37.5) * mm, "end": v(-71.4, -32.61) * mm});
            skLineSegment(sketch, "E46.3.19.0", {"start": v(-82.98, -36.12) * mm, "end": v(-82.37, -37.5) * mm});
            skLineSegment(sketch, "E46.6.19.0", {"start": v(-82.98, -36.12) * mm, "end": v(-72.02, -31.24) * mm});
            skLineSegment(sketch, "E46.9.19.0", {"start": v(-72.02, -31.24) * mm, "end": v(-71.4, -32.61) * mm});
            skLineSegment(sketch, "E46.2.20.0", {"start": v(-78, -45.9) * mm, "end": v(-67.6, -39.9) * mm});
            skLineSegment(sketch, "E46.3.20.0", {"start": v(-78.75, -44.6) * mm, "end": v(-78, -45.9) * mm});
            skLineSegment(sketch, "E46.6.20.0", {"start": v(-78.75, -44.6) * mm, "end": v(-68.36, -38.6) * mm});
            skLineSegment(sketch, "E46.9.20.0", {"start": v(-68.36, -38.6) * mm, "end": v(-67.6, -39.9) * mm});
            skLineSegment(sketch, "E46.2.21.0", {"start": v(-72.78, -53.8) * mm, "end": v(-63.07, -46.75) * mm});
            skLineSegment(sketch, "E46.3.21.0", {"start": v(-73.66, -52.59) * mm, "end": v(-72.78, -53.8) * mm});
            skLineSegment(sketch, "E46.6.21.0", {"start": v(-73.66, -52.59) * mm, "end": v(-63.95, -45.53) * mm});
            skLineSegment(sketch, "E46.9.21.0", {"start": v(-63.95, -45.53) * mm, "end": v(-63.07, -46.75) * mm});
            skLineSegment(sketch, "E46.2.22.0", {"start": v(-66.75, -61.11) * mm, "end": v(-57.84, -53.08) * mm});
            skLineSegment(sketch, "E46.3.22.0", {"start": v(-67.76, -60) * mm, "end": v(-66.75, -61.11) * mm});
            skLineSegment(sketch, "E46.6.22.0", {"start": v(-67.76, -60) * mm, "end": v(-58.84, -51.97) * mm});
            skLineSegment(sketch, "E46.9.22.0", {"start": v(-58.84, -51.97) * mm, "end": v(-57.84, -53.08) * mm});
            skLineSegment(sketch, "E46.2.23.0", {"start": v(-60, -67.76) * mm, "end": v(-51.97, -58.84) * mm});
            skLineSegment(sketch, "E46.3.23.0", {"start": v(-61.11, -66.75) * mm, "end": v(-60, -67.76) * mm});
            skLineSegment(sketch, "E46.6.23.0", {"start": v(-61.11, -66.75) * mm, "end": v(-53.08, -57.84) * mm});
            skLineSegment(sketch, "E46.9.23.0", {"start": v(-53.08, -57.84) * mm, "end": v(-51.97, -58.84) * mm});
            skLineSegment(sketch, "E46.2.24.0", {"start": v(-52.59, -73.66) * mm, "end": v(-45.53, -63.95) * mm});
            skLineSegment(sketch, "E46.3.24.0", {"start": v(-53.8, -72.78) * mm, "end": v(-52.59, -73.66) * mm});
            skLineSegment(sketch, "E46.6.24.0", {"start": v(-53.8, -72.78) * mm, "end": v(-46.75, -63.07) * mm});
            skLineSegment(sketch, "E46.9.24.0", {"start": v(-46.75, -63.07) * mm, "end": v(-45.53, -63.95) * mm});
            skLineSegment(sketch, "E46.2.25.0", {"start": v(-44.6, -78.75) * mm, "end": v(-38.6, -68.36) * mm});
            skLineSegment(sketch, "E46.3.25.0", {"start": v(-45.9, -78) * mm, "end": v(-44.6, -78.75) * mm});
            skLineSegment(sketch, "E46.6.25.0", {"start": v(-45.9, -78) * mm, "end": v(-39.9, -67.6) * mm});
            skLineSegment(sketch, "E46.9.25.0", {"start": v(-39.9, -67.6) * mm, "end": v(-38.6, -68.36) * mm});
            skLineSegment(sketch, "E46.2.26.0", {"start": v(-36.12, -82.98) * mm, "end": v(-31.24, -72.02) * mm});
            skLineSegment(sketch, "E46.3.26.0", {"start": v(-37.5, -82.37) * mm, "end": v(-36.12, -82.98) * mm});
            skLineSegment(sketch, "E46.6.26.0", {"start": v(-37.5, -82.37) * mm, "end": v(-32.61, -71.4) * mm});
            skLineSegment(sketch, "E46.9.26.0", {"start": v(-32.61, -71.4) * mm, "end": v(-31.24, -72.02) * mm});
            skLineSegment(sketch, "E46.2.27.0", {"start": v(-27.25, -86.3) * mm, "end": v(-23.54, -74.89) * mm});
            skLineSegment(sketch, "E46.3.27.0", {"start": v(-28.68, -85.84) * mm, "end": v(-27.25, -86.3) * mm});
            skLineSegment(sketch, "E46.6.27.0", {"start": v(-28.68, -85.84) * mm, "end": v(-24.97, -74.43) * mm});
            skLineSegment(sketch, "E46.9.27.0", {"start": v(-24.97, -74.43) * mm, "end": v(-23.54, -74.89) * mm});
            skLineSegment(sketch, "E46.2.28.0", {"start": v(-18.08, -88.68) * mm, "end": v(-15.59, -76.94) * mm});
            skLineSegment(sketch, "E46.3.28.0", {"start": v(-19.55, -88.37) * mm, "end": v(-18.08, -88.68) * mm});
            skLineSegment(sketch, "E46.6.28.0", {"start": v(-19.55, -88.37) * mm, "end": v(-17.05, -76.63) * mm});
            skLineSegment(sketch, "E46.9.28.0", {"start": v(-17.05, -76.63) * mm, "end": v(-15.59, -76.94) * mm});
            skLineSegment(sketch, "E46.2.29.0", {"start": v(-8.71, -90.08) * mm, "end": v(-7.46, -78.15) * mm});
            skLineSegment(sketch, "E46.3.29.0", {"start": v(-10.2, -89.93) * mm, "end": v(-8.71, -90.08) * mm});
            skLineSegment(sketch, "E46.6.29.0", {"start": v(-10.2, -89.93) * mm, "end": v(-8.95, -78) * mm});
            skLineSegment(sketch, "E46.9.29.0", {"start": v(-8.95, -78) * mm, "end": v(-7.46, -78.15) * mm});
            skLineSegment(sketch, "E46.2.30.0", {"start": v(0.75, -90.5) * mm, "end": v(0.75, -78.5) * mm});
            skLineSegment(sketch, "E46.3.30.0", {"start": v(-0.75, -90.5) * mm, "end": v(0.75, -90.5) * mm});
            skLineSegment(sketch, "E46.6.30.0", {"start": v(-0.75, -90.5) * mm, "end": v(-0.75, -78.5) * mm});
            skLineSegment(sketch, "E46.9.30.0", {"start": v(-0.75, -78.5) * mm, "end": v(0.75, -78.5) * mm});
            skLineSegment(sketch, "E46.2.31.0", {"start": v(10.2, -89.93) * mm, "end": v(8.95, -78) * mm});
            skLineSegment(sketch, "E46.3.31.0", {"start": v(8.71, -90.08) * mm, "end": v(10.2, -89.93) * mm});
            skLineSegment(sketch, "E46.6.31.0", {"start": v(8.71, -90.08) * mm, "end": v(7.46, -78.15) * mm});
            skLineSegment(sketch, "E46.9.31.0", {"start": v(7.46, -78.15) * mm, "end": v(8.95, -78) * mm});
            skLineSegment(sketch, "E46.2.32.0", {"start": v(19.55, -88.37) * mm, "end": v(17.05, -76.63) * mm});
            skLineSegment(sketch, "E46.3.32.0", {"start": v(18.08, -88.68) * mm, "end": v(19.55, -88.37) * mm});
            skLineSegment(sketch, "E46.6.32.0", {"start": v(18.08, -88.68) * mm, "end": v(15.59, -76.94) * mm});
            skLineSegment(sketch, "E46.9.32.0", {"start": v(15.59, -76.94) * mm, "end": v(17.05, -76.63) * mm});
            skLineSegment(sketch, "E46.2.33.0", {"start": v(28.68, -85.84) * mm, "end": v(24.97, -74.43) * mm});
            skLineSegment(sketch, "E46.3.33.0", {"start": v(27.25, -86.3) * mm, "end": v(28.68, -85.84) * mm});
            skLineSegment(sketch, "E46.6.33.0", {"start": v(27.25, -86.3) * mm, "end": v(23.54, -74.89) * mm});
            skLineSegment(sketch, "E46.9.33.0", {"start": v(23.54, -74.89) * mm, "end": v(24.97, -74.43) * mm});
            skLineSegment(sketch, "E46.2.34.0", {"start": v(37.5, -82.37) * mm, "end": v(32.61, -71.4) * mm});
            skLineSegment(sketch, "E46.3.34.0", {"start": v(36.12, -82.98) * mm, "end": v(37.5, -82.37) * mm});
            skLineSegment(sketch, "E46.6.34.0", {"start": v(36.12, -82.98) * mm, "end": v(31.24, -72.02) * mm});
            skLineSegment(sketch, "E46.9.34.0", {"start": v(31.24, -72.02) * mm, "end": v(32.61, -71.4) * mm});
            skLineSegment(sketch, "E46.2.35.0", {"start": v(45.9, -78) * mm, "end": v(39.9, -67.6) * mm});
            skLineSegment(sketch, "E46.3.35.0", {"start": v(44.6, -78.75) * mm, "end": v(45.9, -78) * mm});
            skLineSegment(sketch, "E46.6.35.0", {"start": v(44.6, -78.75) * mm, "end": v(38.6, -68.36) * mm});
            skLineSegment(sketch, "E46.9.35.0", {"start": v(38.6, -68.36) * mm, "end": v(39.9, -67.6) * mm});
            skLineSegment(sketch, "E46.2.36.0", {"start": v(53.8, -72.78) * mm, "end": v(46.75, -63.07) * mm});
            skLineSegment(sketch, "E46.3.36.0", {"start": v(52.59, -73.66) * mm, "end": v(53.8, -72.78) * mm});
            skLineSegment(sketch, "E46.6.36.0", {"start": v(52.59, -73.66) * mm, "end": v(45.53, -63.95) * mm});
            skLineSegment(sketch, "E46.9.36.0", {"start": v(45.53, -63.95) * mm, "end": v(46.75, -63.07) * mm});
            skLineSegment(sketch, "E46.2.37.0", {"start": v(61.11, -66.75) * mm, "end": v(53.08, -57.84) * mm});
            skLineSegment(sketch, "E46.3.37.0", {"start": v(60, -67.76) * mm, "end": v(61.11, -66.75) * mm});
            skLineSegment(sketch, "E46.6.37.0", {"start": v(60, -67.76) * mm, "end": v(51.97, -58.84) * mm});
            skLineSegment(sketch, "E46.9.37.0", {"start": v(51.97, -58.84) * mm, "end": v(53.08, -57.84) * mm});
            skLineSegment(sketch, "E46.2.38.0", {"start": v(67.76, -60) * mm, "end": v(58.84, -51.97) * mm});
            skLineSegment(sketch, "E46.3.38.0", {"start": v(66.75, -61.11) * mm, "end": v(67.76, -60) * mm});
            skLineSegment(sketch, "E46.6.38.0", {"start": v(66.75, -61.11) * mm, "end": v(57.84, -53.08) * mm});
            skLineSegment(sketch, "E46.9.38.0", {"start": v(57.84, -53.08) * mm, "end": v(58.84, -51.97) * mm});
            skLineSegment(sketch, "E46.2.39.0", {"start": v(73.66, -52.59) * mm, "end": v(63.95, -45.53) * mm});
            skLineSegment(sketch, "E46.3.39.0", {"start": v(72.78, -53.8) * mm, "end": v(73.66, -52.59) * mm});
            skLineSegment(sketch, "E46.6.39.0", {"start": v(72.78, -53.8) * mm, "end": v(63.07, -46.75) * mm});
            skLineSegment(sketch, "E46.9.39.0", {"start": v(63.07, -46.75) * mm, "end": v(63.95, -45.53) * mm});
            skLineSegment(sketch, "E46.2.40.0", {"start": v(78.75, -44.6) * mm, "end": v(68.36, -38.6) * mm});
            skLineSegment(sketch, "E46.3.40.0", {"start": v(78, -45.9) * mm, "end": v(78.75, -44.6) * mm});
            skLineSegment(sketch, "E46.6.40.0", {"start": v(78, -45.9) * mm, "end": v(67.6, -39.9) * mm});
            skLineSegment(sketch, "E46.9.40.0", {"start": v(67.6, -39.9) * mm, "end": v(68.36, -38.6) * mm});
            skLineSegment(sketch, "E46.2.41.0", {"start": v(82.98, -36.12) * mm, "end": v(72.02, -31.24) * mm});
            skLineSegment(sketch, "E46.3.41.0", {"start": v(82.37, -37.5) * mm, "end": v(82.98, -36.12) * mm});
            skLineSegment(sketch, "E46.6.41.0", {"start": v(82.37, -37.5) * mm, "end": v(71.4, -32.61) * mm});
            skLineSegment(sketch, "E46.9.41.0", {"start": v(71.4, -32.61) * mm, "end": v(72.02, -31.24) * mm});
            skLineSegment(sketch, "E46.2.42.0", {"start": v(86.3, -27.25) * mm, "end": v(74.89, -23.54) * mm});
            skLineSegment(sketch, "E46.3.42.0", {"start": v(85.84, -28.68) * mm, "end": v(86.3, -27.25) * mm});
            skLineSegment(sketch, "E46.6.42.0", {"start": v(85.84, -28.68) * mm, "end": v(74.43, -24.97) * mm});
            skLineSegment(sketch, "E46.9.42.0", {"start": v(74.43, -24.97) * mm, "end": v(74.89, -23.54) * mm});
            skLineSegment(sketch, "E46.2.43.0", {"start": v(88.68, -18.08) * mm, "end": v(76.94, -15.59) * mm});
            skLineSegment(sketch, "E46.3.43.0", {"start": v(88.37, -19.55) * mm, "end": v(88.68, -18.08) * mm});
            skLineSegment(sketch, "E46.6.43.0", {"start": v(88.37, -19.55) * mm, "end": v(76.63, -17.05) * mm});
            skLineSegment(sketch, "E46.9.43.0", {"start": v(76.63, -17.05) * mm, "end": v(76.94, -15.59) * mm});
            skLineSegment(sketch, "E46.2.44.0", {"start": v(90.08, -8.71) * mm, "end": v(78.15, -7.46) * mm});
            skLineSegment(sketch, "E46.3.44.0", {"start": v(89.93, -10.2) * mm, "end": v(90.08, -8.71) * mm});
            skLineSegment(sketch, "E46.6.44.0", {"start": v(89.93, -10.2) * mm, "end": v(78, -8.95) * mm});
            skLineSegment(sketch, "E46.9.44.0", {"start": v(78, -8.95) * mm, "end": v(78.15, -7.46) * mm});
            skLineSegment(sketch, "E46.2.45.0", {"start": v(90.5, 0.75) * mm, "end": v(78.5, 0.75) * mm});
            skLineSegment(sketch, "E46.3.45.0", {"start": v(90.5, -0.75) * mm, "end": v(90.5, 0.75) * mm});
            skLineSegment(sketch, "E46.6.45.0", {"start": v(90.5, -0.75) * mm, "end": v(78.5, -0.75) * mm});
            skLineSegment(sketch, "E46.9.45.0", {"start": v(78.5, -0.75) * mm, "end": v(78.5, 0.75) * mm});
            skLineSegment(sketch, "E46.2.46.0", {"start": v(89.93, 10.2) * mm, "end": v(78, 8.95) * mm});
            skLineSegment(sketch, "E46.3.46.0", {"start": v(90.08, 8.71) * mm, "end": v(89.93, 10.2) * mm});
            skLineSegment(sketch, "E46.6.46.0", {"start": v(90.08, 8.71) * mm, "end": v(78.15, 7.46) * mm});
            skLineSegment(sketch, "E46.9.46.0", {"start": v(78.15, 7.46) * mm, "end": v(78, 8.95) * mm});
            skLineSegment(sketch, "E46.2.47.0", {"start": v(88.37, 19.55) * mm, "end": v(76.63, 17.05) * mm});
            skLineSegment(sketch, "E46.3.47.0", {"start": v(88.68, 18.08) * mm, "end": v(88.37, 19.55) * mm});
            skLineSegment(sketch, "E46.6.47.0", {"start": v(88.68, 18.08) * mm, "end": v(76.94, 15.59) * mm});
            skLineSegment(sketch, "E46.9.47.0", {"start": v(76.94, 15.59) * mm, "end": v(76.63, 17.05) * mm});
            skLineSegment(sketch, "E46.2.48.0", {"start": v(85.84, 28.68) * mm, "end": v(74.43, 24.97) * mm});
            skLineSegment(sketch, "E46.3.48.0", {"start": v(86.3, 27.25) * mm, "end": v(85.84, 28.68) * mm});
            skLineSegment(sketch, "E46.6.48.0", {"start": v(86.3, 27.25) * mm, "end": v(74.89, 23.54) * mm});
            skLineSegment(sketch, "E46.9.48.0", {"start": v(74.89, 23.54) * mm, "end": v(74.43, 24.97) * mm});
            skLineSegment(sketch, "E46.2.49.0", {"start": v(82.37, 37.5) * mm, "end": v(71.4, 32.61) * mm});
            skLineSegment(sketch, "E46.3.49.0", {"start": v(82.98, 36.12) * mm, "end": v(82.37, 37.5) * mm});
            skLineSegment(sketch, "E46.6.49.0", {"start": v(82.98, 36.12) * mm, "end": v(72.02, 31.24) * mm});
            skLineSegment(sketch, "E46.9.49.0", {"start": v(72.02, 31.24) * mm, "end": v(71.4, 32.61) * mm});
            skLineSegment(sketch, "E46.2.50.0", {"start": v(78, 45.9) * mm, "end": v(67.6, 39.9) * mm});
            skLineSegment(sketch, "E46.3.50.0", {"start": v(78.75, 44.6) * mm, "end": v(78, 45.9) * mm});
            skLineSegment(sketch, "E46.6.50.0", {"start": v(78.75, 44.6) * mm, "end": v(68.36, 38.6) * mm});
            skLineSegment(sketch, "E46.9.50.0", {"start": v(68.36, 38.6) * mm, "end": v(67.6, 39.9) * mm});
            skLineSegment(sketch, "E46.2.51.0", {"start": v(72.78, 53.8) * mm, "end": v(63.07, 46.75) * mm});
            skLineSegment(sketch, "E46.3.51.0", {"start": v(73.66, 52.59) * mm, "end": v(72.78, 53.8) * mm});
            skLineSegment(sketch, "E46.6.51.0", {"start": v(73.66, 52.59) * mm, "end": v(63.95, 45.53) * mm});
            skLineSegment(sketch, "E46.9.51.0", {"start": v(63.95, 45.53) * mm, "end": v(63.07, 46.75) * mm});
            skLineSegment(sketch, "E46.2.52.0", {"start": v(66.75, 61.11) * mm, "end": v(57.84, 53.08) * mm});
            skLineSegment(sketch, "E46.3.52.0", {"start": v(67.76, 60) * mm, "end": v(66.75, 61.11) * mm});
            skLineSegment(sketch, "E46.6.52.0", {"start": v(67.76, 60) * mm, "end": v(58.84, 51.97) * mm});
            skLineSegment(sketch, "E46.9.52.0", {"start": v(58.84, 51.97) * mm, "end": v(57.84, 53.08) * mm});
            skLineSegment(sketch, "E46.2.53.0", {"start": v(60, 67.76) * mm, "end": v(51.97, 58.84) * mm});
            skLineSegment(sketch, "E46.3.53.0", {"start": v(61.11, 66.75) * mm, "end": v(60, 67.76) * mm});
            skLineSegment(sketch, "E46.6.53.0", {"start": v(61.11, 66.75) * mm, "end": v(53.08, 57.84) * mm});
            skLineSegment(sketch, "E46.9.53.0", {"start": v(53.08, 57.84) * mm, "end": v(51.97, 58.84) * mm});
            skLineSegment(sketch, "E46.2.54.0", {"start": v(52.59, 73.66) * mm, "end": v(45.53, 63.95) * mm});
            skLineSegment(sketch, "E46.3.54.0", {"start": v(53.8, 72.78) * mm, "end": v(52.59, 73.66) * mm});
            skLineSegment(sketch, "E46.6.54.0", {"start": v(53.8, 72.78) * mm, "end": v(46.75, 63.07) * mm});
            skLineSegment(sketch, "E46.9.54.0", {"start": v(46.75, 63.07) * mm, "end": v(45.53, 63.95) * mm});
            skLineSegment(sketch, "E46.2.55.0", {"start": v(44.6, 78.75) * mm, "end": v(38.6, 68.36) * mm});
            skLineSegment(sketch, "E46.3.55.0", {"start": v(45.9, 78) * mm, "end": v(44.6, 78.75) * mm});
            skLineSegment(sketch, "E46.6.55.0", {"start": v(45.9, 78) * mm, "end": v(39.9, 67.6) * mm});
            skLineSegment(sketch, "E46.9.55.0", {"start": v(39.9, 67.6) * mm, "end": v(38.6, 68.36) * mm});
            skLineSegment(sketch, "E46.2.56.0", {"start": v(36.12, 82.98) * mm, "end": v(31.24, 72.02) * mm});
            skLineSegment(sketch, "E46.3.56.0", {"start": v(37.5, 82.37) * mm, "end": v(36.12, 82.98) * mm});
            skLineSegment(sketch, "E46.6.56.0", {"start": v(37.5, 82.37) * mm, "end": v(32.61, 71.4) * mm});
            skLineSegment(sketch, "E46.9.56.0", {"start": v(32.61, 71.4) * mm, "end": v(31.24, 72.02) * mm});
            skLineSegment(sketch, "E46.2.57.0", {"start": v(27.25, 86.3) * mm, "end": v(23.54, 74.89) * mm});
            skLineSegment(sketch, "E46.3.57.0", {"start": v(28.68, 85.84) * mm, "end": v(27.25, 86.3) * mm});
            skLineSegment(sketch, "E46.6.57.0", {"start": v(28.68, 85.84) * mm, "end": v(24.97, 74.43) * mm});
            skLineSegment(sketch, "E46.9.57.0", {"start": v(24.97, 74.43) * mm, "end": v(23.54, 74.89) * mm});
            skLineSegment(sketch, "E46.2.58.0", {"start": v(18.08, 88.68) * mm, "end": v(15.59, 76.94) * mm});
            skLineSegment(sketch, "E46.3.58.0", {"start": v(19.55, 88.37) * mm, "end": v(18.08, 88.68) * mm});
            skLineSegment(sketch, "E46.6.58.0", {"start": v(19.55, 88.37) * mm, "end": v(17.05, 76.63) * mm});
            skLineSegment(sketch, "E46.9.58.0", {"start": v(17.05, 76.63) * mm, "end": v(15.59, 76.94) * mm});
            skLineSegment(sketch, "E46.2.59.0", {"start": v(8.71, 90.08) * mm, "end": v(7.46, 78.15) * mm});
            skLineSegment(sketch, "E46.3.59.0", {"start": v(10.2, 89.93) * mm, "end": v(8.71, 90.08) * mm});
            skLineSegment(sketch, "E46.6.59.0", {"start": v(10.2, 89.93) * mm, "end": v(8.95, 78) * mm});
            skLineSegment(sketch, "E46.9.59.0", {"start": v(8.95, 78) * mm, "end": v(7.46, 78.15) * mm});
            skSolve(sketch);
        }
        {
            var Q0;
            Q0 = qSketchRegion(id + "F27", true);
            extrude(context, id + "F28", {"entities" : qUnion([Q0]), "operationType" : NewBodyOperationType.REMOVE, "oppositeDirection" : true, "depth" : 0.2 * mm, "offsetDistance" : 25 * mm});
        }
        {
            var Q0;
            Q0=makeQuery(id+"F26.boolean.opBoolean","COPY",FACE,{"derivedFrom":makeQuery(id+"F26.opExtrude","CAP_FACE",FACE,{"disambiguationData":[OSD([sQuery(id+"F25.wireOp",EDGE,"E41.bottom"),sQuery(id+"F25.wireOp",EDGE,"E41.top"),sQuery(id+"F25.wireOp",EDGE,"E41.left"),sQuery(id+"F25.wireOp",EDGE,"E41.right")])],"isStart":false})});
            extrude(context, id + "F29", {"entities" : qUnion([Q0]), "depth" : 1 * mm, "offsetDistance" : 25 * mm});
        }
        {
            var Q0;
            Q0=makeQuery(id+"F28.boolean.opBoolean","COPY",FACE,{"derivedFrom":makeQuery(id+"F28.opExtrude","CAP_FACE",FACE,{"disambiguationData":[OSD([sQuery(id+"F27.wireOp",EDGE,"E46.2.59.0"),sQuery(id+"F27.wireOp",EDGE,"E46.3.59.0"),sQuery(id+"F27.wireOp",EDGE,"E46.6.59.0"),sQuery(id+"F27.wireOp",EDGE,"E46.9.59.0")])],"isStart":false})});
            extrude(context, id + "F30", {"entities" : qUnion([Q0]), "depth" : 0.4 * mm, "offsetDistance" : 25 * mm});
        }
        {
            var Q0;
            Q0=makeQuery(id+"F15.opExtrude","CAP_FACE",FACE,{"disambiguationData":[OSD([sQuery(id+"F14.wireOp",EDGE,"E21.0.0"),sQuery(id+"F14.wireOp",EDGE,"E22"),sQuery(id+"F14.wireOp",EDGE,"E23"),sQuery(id+"F14.wireOp",EDGE,"E24"),sQuery(id+"F14.wireOp",EDGE,"E25.MirrorCS"),sQuery(id+"F14.wireOp",EDGE,"E26.MirrorCS"),sQuery(id+"F14.wireOp",EDGE,"E27.1.0"),sQuery(id+"F14.wireOp",EDGE,"E27.1.1"),sQuery(id+"F14.wireOp",EDGE,"E27.1.2"),sQuery(id+"F14.wireOp",EDGE,"E27.1.3"),sQuery(id+"F14.wireOp",EDGE,"E27.2.0"),sQuery(id+"F14.wireOp",EDGE,"E27.2.1"),sQuery(id+"F14.wireOp",EDGE,"E27.2.2"),sQuery(id+"F14.wireOp",EDGE,"E27.2.3"),sQuery(id+"F14.wireOp",EDGE,"E28.2.3.0"),sQuery(id+"F14.wireOp",EDGE,"E28.3.3.0"),sQuery(id+"F14.wireOp",EDGE,"E28.6.3.0"),sQuery(id+"F14.wireOp",EDGE,"E28.9.3.0"),sQuery(id+"F14.wireOp",EDGE,"E28.2.4.0"),sQuery(id+"F14.wireOp",EDGE,"E28.3.4.0"),sQuery(id+"F14.wireOp",EDGE,"E28.6.4.0"),sQuery(id+"F14.wireOp",EDGE,"E28.9.4.0"),sQuery(id+"F14.wireOp",EDGE,"E28.2.5.0"),sQuery(id+"F14.wireOp",EDGE,"E28.3.5.0"),sQuery(id+"F14.wireOp",EDGE,"E28.6.5.0"),sQuery(id+"F14.wireOp",EDGE,"E28.9.5.0"),sQuery(id+"F14.wireOp",EDGE,"E28.2.6.0"),sQuery(id+"F14.wireOp",EDGE,"E28.3.6.0"),sQuery(id+"F14.wireOp",EDGE,"E28.6.6.0"),sQuery(id+"F14.wireOp",EDGE,"E28.9.6.0"),sQuery(id+"F14.wireOp",EDGE,"E28.2.7.0"),sQuery(id+"F14.wireOp",EDGE,"E28.3.7.0"),sQuery(id+"F14.wireOp",EDGE,"E28.6.7.0"),sQuery(id+"F14.wireOp",EDGE,"E28.9.7.0"),sQuery(id+"F14.wireOp",EDGE,"E28.2.8.0"),sQuery(id+"F14.wireOp",EDGE,"E28.3.8.0"),sQuery(id+"F14.wireOp",EDGE,"E28.6.8.0"),sQuery(id+"F14.wireOp",EDGE,"E28.9.8.0"),sQuery(id+"F14.wireOp",EDGE,"E28.2.9.0"),sQuery(id+"F14.wireOp",EDGE,"E28.3.9.0"),sQuery(id+"F14.wireOp",EDGE,"E28.6.9.0"),sQuery(id+"F14.wireOp",EDGE,"E28.9.9.0"),sQuery(id+"F14.wireOp",EDGE,"E28.2.10.0"),sQuery(id+"F14.wireOp",EDGE,"E28.3.10.0"),sQuery(id+"F14.wireOp",EDGE,"E28.6.10.0"),sQuery(id+"F14.wireOp",EDGE,"E28.9.10.0"),sQuery(id+"F14.wireOp",EDGE,"E28.2.11.0"),sQuery(id+"F14.wireOp",EDGE,"E28.3.11.0"),sQuery(id+"F14.wireOp",EDGE,"E28.6.11.0"),sQuery(id+"F14.wireOp",EDGE,"E28.9.11.0"),sQuery(id+"F14.wireOp",EDGE,"E28.2.12.0"),sQuery(id+"F14.wireOp",EDGE,"E28.3.12.0"),sQuery(id+"F14.wireOp",EDGE,"E28.6.12.0"),sQuery(id+"F14.wireOp",EDGE,"E28.9.12.0"),sQuery(id+"F14.wireOp",EDGE,"E28.2.13.0"),sQuery(id+"F14.wireOp",EDGE,"E28.3.13.0"),sQuery(id+"F14.wireOp",EDGE,"E28.6.13.0"),sQuery(id+"F14.wireOp",EDGE,"E28.9.13.0"),sQuery(id+"F14.wireOp",EDGE,"E28.2.14.0"),sQuery(id+"F14.wireOp",EDGE,"E28.3.14.0"),sQuery(id+"F14.wireOp",EDGE,"E28.6.14.0"),sQuery(id+"F14.wireOp",EDGE,"E28.9.14.0"),sQuery(id+"F14.wireOp",EDGE,"E28.2.15.0"),sQuery(id+"F14.wireOp",EDGE,"E28.3.15.0"),sQuery(id+"F14.wireOp",EDGE,"E28.6.15.0"),sQuery(id+"F14.wireOp",EDGE,"E28.9.15.0"),sQuery(id+"F14.wireOp",EDGE,"E28.2.16.0"),sQuery(id+"F14.wireOp",EDGE,"E28.3.16.0"),sQuery(id+"F14.wireOp",EDGE,"E28.6.16.0"),sQuery(id+"F14.wireOp",EDGE,"E28.9.16.0"),sQuery(id+"F14.wireOp",EDGE,"E28.2.17.0"),sQuery(id+"F14.wireOp",EDGE,"E28.3.17.0"),sQuery(id+"F14.wireOp",EDGE,"E28.6.17.0"),sQuery(id+"F14.wireOp",EDGE,"E28.9.17.0"),sQuery(id+"F14.wireOp",EDGE,"E28.2.18.0"),sQuery(id+"F14.wireOp",EDGE,"E28.3.18.0"),sQuery(id+"F14.wireOp",EDGE,"E28.6.18.0"),sQuery(id+"F14.wireOp",EDGE,"E28.9.18.0"),sQuery(id+"F14.wireOp",EDGE,"E28.2.19.0"),sQuery(id+"F14.wireOp",EDGE,"E28.3.19.0"),sQuery(id+"F14.wireOp",EDGE,"E28.6.19.0"),sQuery(id+"F14.wireOp",EDGE,"E28.9.19.0"),sQuery(id+"F14.wireOp",EDGE,"E28.2.20.0"),sQuery(id+"F14.wireOp",EDGE,"E28.3.20.0"),sQuery(id+"F14.wireOp",EDGE,"E28.6.20.0"),sQuery(id+"F14.wireOp",EDGE,"E28.9.20.0"),sQuery(id+"F14.wireOp",EDGE,"E28.2.21.0"),sQuery(id+"F14.wireOp",EDGE,"E28.3.21.0"),sQuery(id+"F14.wireOp",EDGE,"E28.6.21.0"),sQuery(id+"F14.wireOp",EDGE,"E28.9.21.0"),sQuery(id+"F14.wireOp",EDGE,"E28.2.22.0"),sQuery(id+"F14.wireOp",EDGE,"E28.3.22.0"),sQuery(id+"F14.wireOp",EDGE,"E28.6.22.0"),sQuery(id+"F14.wireOp",EDGE,"E28.9.22.0"),sQuery(id+"F14.wireOp",EDGE,"E28.2.23.0"),sQuery(id+"F14.wireOp",EDGE,"E28.3.23.0"),sQuery(id+"F14.wireOp",EDGE,"E28.6.23.0"),sQuery(id+"F14.wireOp",EDGE,"E28.9.23.0"),sQuery(id+"F14.wireOp",EDGE,"E28.2.24.0"),sQuery(id+"F14.wireOp",EDGE,"E28.3.24.0"),sQuery(id+"F14.wireOp",EDGE,"E28.6.24.0"),sQuery(id+"F14.wireOp",EDGE,"E28.9.24.0"),sQuery(id+"F14.wireOp",EDGE,"E28.2.25.0"),sQuery(id+"F14.wireOp",EDGE,"E28.3.25.0"),sQuery(id+"F14.wireOp",EDGE,"E28.6.25.0"),sQuery(id+"F14.wireOp",EDGE,"E28.9.25.0"),sQuery(id+"F14.wireOp",EDGE,"E28.2.26.0"),sQuery(id+"F14.wireOp",EDGE,"E28.3.26.0"),sQuery(id+"F14.wireOp",EDGE,"E28.6.26.0"),sQuery(id+"F14.wireOp",EDGE,"E28.9.26.0"),sQuery(id+"F14.wireOp",EDGE,"E28.2.27.0"),sQuery(id+"F14.wireOp",EDGE,"E28.3.27.0"),sQuery(id+"F14.wireOp",EDGE,"E28.6.27.0"),sQuery(id+"F14.wireOp",EDGE,"E28.9.27.0"),sQuery(id+"F14.wireOp",EDGE,"E28.2.28.0"),sQuery(id+"F14.wireOp",EDGE,"E28.3.28.0"),sQuery(id+"F14.wireOp",EDGE,"E28.6.28.0"),sQuery(id+"F14.wireOp",EDGE,"E28.9.28.0"),sQuery(id+"F14.wireOp",EDGE,"E28.2.29.0"),sQuery(id+"F14.wireOp",EDGE,"E28.3.29.0"),sQuery(id+"F14.wireOp",EDGE,"E28.6.29.0"),sQuery(id+"F14.wireOp",EDGE,"E28.9.29.0"),sQuery(id+"F14.wireOp",EDGE,"E28.2.30.0"),sQuery(id+"F14.wireOp",EDGE,"E28.3.30.0"),sQuery(id+"F14.wireOp",EDGE,"E28.6.30.0"),sQuery(id+"F14.wireOp",EDGE,"E28.9.30.0"),sQuery(id+"F14.wireOp",EDGE,"E28.2.31.0"),sQuery(id+"F14.wireOp",EDGE,"E28.3.31.0"),sQuery(id+"F14.wireOp",EDGE,"E28.6.31.0"),sQuery(id+"F14.wireOp",EDGE,"E28.9.31.0"),sQuery(id+"F14.wireOp",EDGE,"E28.2.32.0"),sQuery(id+"F14.wireOp",EDGE,"E28.3.32.0"),sQuery(id+"F14.wireOp",EDGE,"E28.6.32.0"),sQuery(id+"F14.wireOp",EDGE,"E28.9.32.0"),sQuery(id+"F14.wireOp",EDGE,"E28.2.33.0"),sQuery(id+"F14.wireOp",EDGE,"E28.3.33.0"),sQuery(id+"F14.wireOp",EDGE,"E28.6.33.0"),sQuery(id+"F14.wireOp",EDGE,"E28.9.33.0"),sQuery(id+"F14.wireOp",EDGE,"E28.2.34.0"),sQuery(id+"F14.wireOp",EDGE,"E28.3.34.0"),sQuery(id+"F14.wireOp",EDGE,"E28.6.34.0"),sQuery(id+"F14.wireOp",EDGE,"E28.9.34.0"),sQuery(id+"F14.wireOp",EDGE,"E28.2.35.0"),sQuery(id+"F14.wireOp",EDGE,"E28.3.35.0"),sQuery(id+"F14.wireOp",EDGE,"E28.6.35.0"),sQuery(id+"F14.wireOp",EDGE,"E28.9.35.0"),sQuery(id+"F14.wireOp",EDGE,"E28.2.36.0"),sQuery(id+"F14.wireOp",EDGE,"E28.3.36.0"),sQuery(id+"F14.wireOp",EDGE,"E28.6.36.0"),sQuery(id+"F14.wireOp",EDGE,"E28.9.36.0"),sQuery(id+"F14.wireOp",EDGE,"E28.2.37.0"),sQuery(id+"F14.wireOp",EDGE,"E28.3.37.0"),sQuery(id+"F14.wireOp",EDGE,"E28.6.37.0"),sQuery(id+"F14.wireOp",EDGE,"E28.9.37.0"),sQuery(id+"F14.wireOp",EDGE,"E28.2.38.0"),sQuery(id+"F14.wireOp",EDGE,"E28.3.38.0"),sQuery(id+"F14.wireOp",EDGE,"E28.6.38.0"),sQuery(id+"F14.wireOp",EDGE,"E28.9.38.0"),sQuery(id+"F14.wireOp",EDGE,"E28.2.39.0"),sQuery(id+"F14.wireOp",EDGE,"E28.3.39.0"),sQuery(id+"F14.wireOp",EDGE,"E28.6.39.0"),sQuery(id+"F14.wireOp",EDGE,"E28.9.39.0")])],"isStart":false});
            var sketch = newSketch(context, id + "F31", { "sketchPlane" : qUnion([Q0])});
            skCircle(sketch, "E47.0", {"center": v(0, 0) * mm, "radius": 3 * mm});
            skCircle(sketch, "E48.0", {"center": v(0, 0) * mm, "radius": 5 * mm});
            skSolve(sketch);
        }
        {
            var Q0;
            Q0 = qSketchRegion(id + "F31", true);
            extrude(context, id + "F32", {"entities" : qUnion([Q0]), "operationType" : NewBodyOperationType.ADD, "depth" : 5 * mm, "offsetDistance" : 25 * mm});
        }
        {
            var Q0;
            Q0=makeQuery(id+"F32.opExtrude","CAP_FACE",FACE,{"disambiguationData":[OSD([sQuery(id+"F31.wireOp",EDGE,"E47.0"),sQuery(id+"F31.wireOp",EDGE,"E48.0")])],"isStart":false});
            var sketch = newSketch(context, id + "F33", { "sketchPlane" : qUnion([Q0])});
            skCircle(sketch, "E49.0", {"center": v(0, 0) * mm, "radius": 5 * mm});
            skCircle(sketch, "E50.0", {"center": v(0, 0) * mm, "radius": 3 * mm});
            skLineSegment(sketch, "E51", {"start": v(0, 50) * mm, "end": v(1.5, 50) * mm});
            skLineSegment(sketch, "E52", {"start": v(1.5, 50) * mm, "end": v(3, 4) * mm});
            skLineSegment(sketch, "E53.MirrorCS", {"start": v(0, 50) * mm, "end": v(-1.5, 50) * mm});
            skLineSegment(sketch, "E54.MirrorCS", {"start": v(-1.5, 50) * mm, "end": v(-3, 4) * mm});
            skSolve(sketch);
        }
        {
            var Q0;
            Q0 = qSketchRegion(id + "F33", true);
            extrude(context, id + "F34", {"entities" : qUnion([Q0]), "operationType" : NewBodyOperationType.ADD, "depth" : 1 * mm, "offsetDistance" : 25 * mm});
        }
        {
            var Q0;
            Q0=makeQuery(id+"F6.opExtrude","CAP_FACE",FACE,{"disambiguationData":[OSD([sQuery(id+"F0.wireOp",EDGE,"E0")])],"isStart":false});
            var sketch = newSketch(context, id + "F35", { "sketchPlane" : qUnion([Q0])});
            skCircle(sketch, "E55", {"center": v(0, 0) * mm, "radius": 5 * mm});
            skLineSegment(sketch, "E56", {"start": v(0, 80) * mm, "end": v(0.5, 80) * mm});
            skLineSegment(sketch, "E57", {"start": v(0.5, 80) * mm, "end": v(2, 4.58) * mm});
            skLineSegment(sketch, "E58.MirrorCS", {"start": v(0, 80) * mm, "end": v(-0.5, 80) * mm});
            skLineSegment(sketch, "E59.MirrorCS", {"start": v(-0.5, 80) * mm, "end": v(-2, 4.58) * mm});
            skSolve(sketch);
        }
        {
            var Q0;
            Q0 = qSketchRegion(id + "F35", true);
            extrude(context, id + "F36", {"entities" : qUnion([Q0]), "operationType" : NewBodyOperationType.ADD, "oppositeDirection" : true, "depth" : 1 * mm, "offsetDistance" : 25 * mm});
        }
    });
